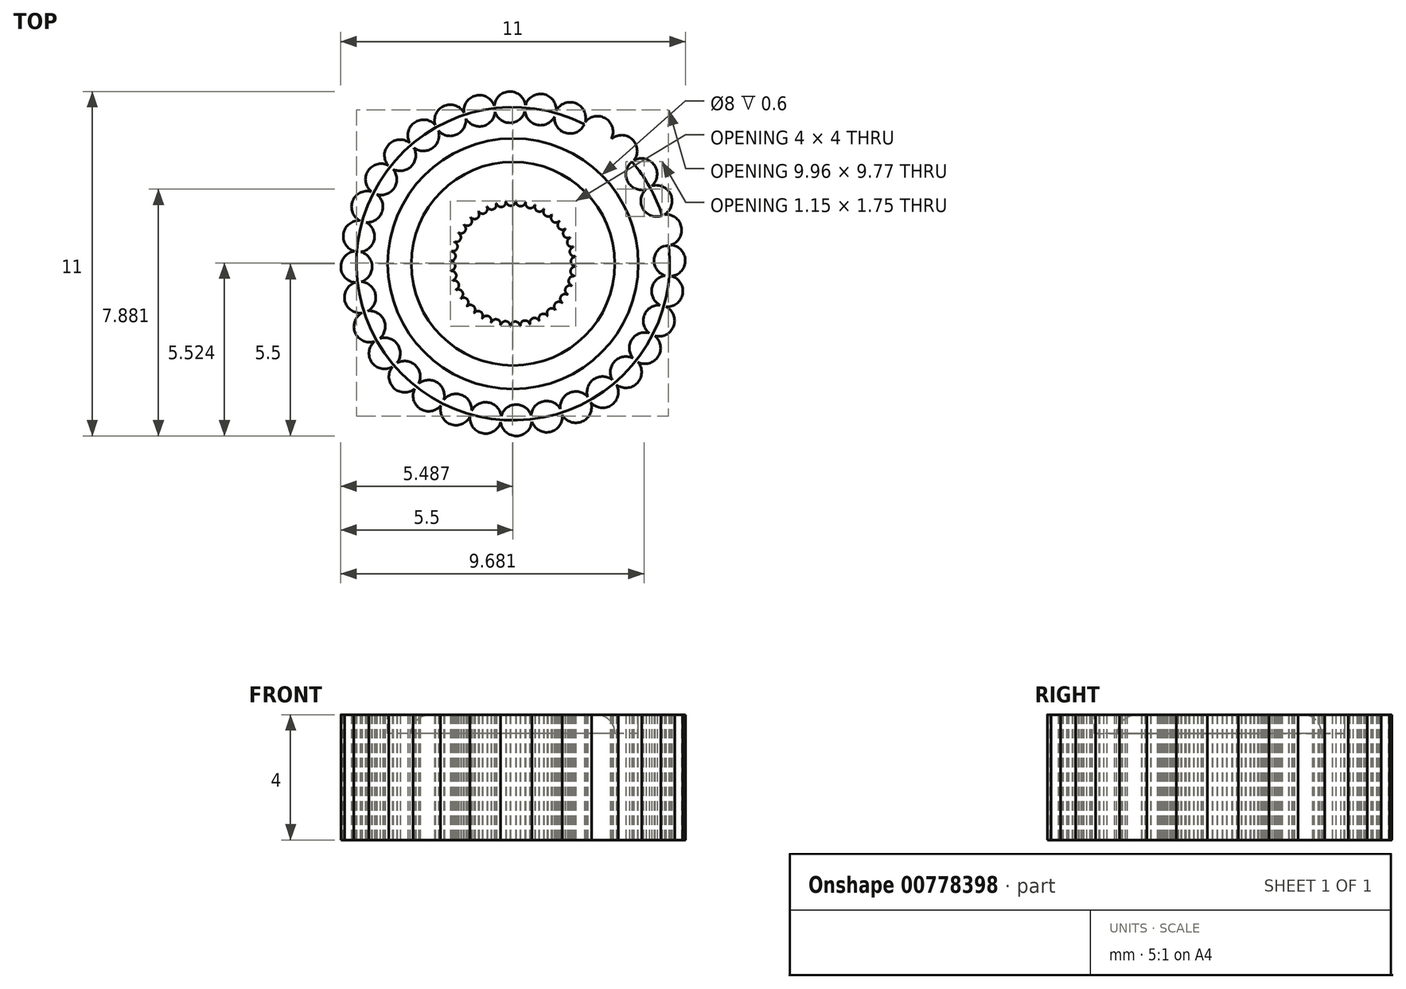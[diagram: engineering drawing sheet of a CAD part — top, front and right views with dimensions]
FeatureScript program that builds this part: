
annotation { "Feature Type Name" : "Feature", "Feature Type Description" : "" }
export const myFeature = defineFeature(function(context is Context, id is Id, definition is map)
    precondition{}
    {
        {
            var Q0;
            Q0=qCreatedBy(makeId("Top.planeOp"),FACE);
            var sketch = newSketch(context, id + "F0", { "sketchPlane" : qUnion([Q0])});
            skCircle(sketch, "E0", {"center": v(0, 0) * mm, "radius": 5 * mm});
            skCircle(sketch, "E1", {"center": v(0, 0) * mm, "radius": 2 * mm});
            skCircle(sketch, "E2", {"center": v(2.7, 4.21) * mm, "radius": 0.5 * mm});
            skCircle(sketch, "E3.1.0", {"center": v(1.82, 4.66) * mm, "radius": 0.5 * mm});
            skCircle(sketch, "E3.2.0", {"center": v(0.88, 4.92) * mm, "radius": 0.5 * mm});
            skCircle(sketch, "E4.1.3.0", {"center": v(-0.1, 5) * mm, "radius": 0.5 * mm});
            skCircle(sketch, "E4.1.4.0", {"center": v(-1.07, 4.88) * mm, "radius": 0.5 * mm});
            skCircle(sketch, "E4.1.5.0", {"center": v(-2, 4.58) * mm, "radius": 0.5 * mm});
            skCircle(sketch, "E4.1.6.0", {"center": v(-2.86, 4.1) * mm, "radius": 0.5 * mm});
            skCircle(sketch, "E4.1.7.0", {"center": v(-3.6, 3.46) * mm, "radius": 0.5 * mm});
            skCircle(sketch, "E4.1.8.0", {"center": v(-4.21, 2.7) * mm, "radius": 0.5 * mm});
            skCircle(sketch, "E4.1.9.0", {"center": v(-4.66, 1.82) * mm, "radius": 0.5 * mm});
            skCircle(sketch, "E5.1.10.0", {"center": v(-4.92, 0.88) * mm, "radius": 0.5 * mm});
            skCircle(sketch, "E5.1.11.0", {"center": v(-5, -0.1) * mm, "radius": 0.5 * mm});
            skCircle(sketch, "E5.1.12.0", {"center": v(-4.88, -1.07) * mm, "radius": 0.5 * mm});
            skCircle(sketch, "E5.1.13.0", {"center": v(-4.58, -2) * mm, "radius": 0.5 * mm});
            skCircle(sketch, "E5.1.14.0", {"center": v(-4.1, -2.86) * mm, "radius": 0.5 * mm});
            skCircle(sketch, "E5.1.15.0", {"center": v(-3.46, -3.6) * mm, "radius": 0.5 * mm});
            skCircle(sketch, "E5.1.16.0", {"center": v(-2.7, -4.21) * mm, "radius": 0.5 * mm});
            skCircle(sketch, "E5.1.17.0", {"center": v(-1.82, -4.66) * mm, "radius": 0.5 * mm});
            skCircle(sketch, "E5.1.18.0", {"center": v(-0.88, -4.92) * mm, "radius": 0.5 * mm});
            skCircle(sketch, "E5.1.19.0", {"center": v(0.1, -5) * mm, "radius": 0.5 * mm});
            skCircle(sketch, "E5.1.20.0", {"center": v(1.07, -4.88) * mm, "radius": 0.5 * mm});
            skCircle(sketch, "E5.1.21.0", {"center": v(2, -4.58) * mm, "radius": 0.5 * mm});
            skCircle(sketch, "E5.1.22.0", {"center": v(2.86, -4.1) * mm, "radius": 0.5 * mm});
            skCircle(sketch, "E5.1.23.0", {"center": v(3.6, -3.46) * mm, "radius": 0.5 * mm});
            skCircle(sketch, "E5.1.24.0", {"center": v(4.21, -2.7) * mm, "radius": 0.5 * mm});
            skCircle(sketch, "E5.1.25.0", {"center": v(4.66, -1.82) * mm, "radius": 0.5 * mm});
            skCircle(sketch, "E5.1.26.0", {"center": v(4.92, -0.88) * mm, "radius": 0.5 * mm});
            skCircle(sketch, "E5.1.27.0", {"center": v(5, 0.1) * mm, "radius": 0.5 * mm});
            skCircle(sketch, "E5.1.28.0", {"center": v(4.88, 1.07) * mm, "radius": 0.5 * mm});
            skCircle(sketch, "E5.1.29.0", {"center": v(4.58, 2) * mm, "radius": 0.5 * mm});
            skCircle(sketch, "E5.1.30.0", {"center": v(4.1, 2.86) * mm, "radius": 0.5 * mm});
            skCircle(sketch, "E5.1.31.0", {"center": v(3.46, 3.6) * mm, "radius": 0.5 * mm});
            skCircle(sketch, "E6", {"center": v(1.36, 1.46) * mm, "radius": 0.15 * mm});
            skCircle(sketch, "E7.1.0", {"center": v(1.12, 1.66) * mm, "radius": 0.15 * mm});
            skCircle(sketch, "E7.2.0", {"center": v(0.84, 1.81) * mm, "radius": 0.15 * mm});
            skCircle(sketch, "E7.3.0", {"center": v(0.55, 1.92) * mm, "radius": 0.15 * mm});
            skCircle(sketch, "E7.4.0", {"center": v(0.24, 1.99) * mm, "radius": 0.15 * mm});
            skCircle(sketch, "E7.5.0", {"center": v(-0.07, 2) * mm, "radius": 0.15 * mm});
            skCircle(sketch, "E7.6.0", {"center": v(-0.38, 1.96) * mm, "radius": 0.15 * mm});
            skCircle(sketch, "E7.7.0", {"center": v(-0.69, 1.88) * mm, "radius": 0.15 * mm});
            skCircle(sketch, "E7.8.0", {"center": v(-0.97, 1.75) * mm, "radius": 0.15 * mm});
            skCircle(sketch, "E7.9.0", {"center": v(-1.23, 1.57) * mm, "radius": 0.15 * mm});
            skCircle(sketch, "E7.10.0", {"center": v(-1.46, 1.36) * mm, "radius": 0.15 * mm});
            skCircle(sketch, "E7.11.0", {"center": v(-1.66, 1.12) * mm, "radius": 0.15 * mm});
            skCircle(sketch, "E7.12.0", {"center": v(-1.81, 0.84) * mm, "radius": 0.15 * mm});
            skCircle(sketch, "E7.13.0", {"center": v(-1.92, 0.55) * mm, "radius": 0.15 * mm});
            skCircle(sketch, "E7.14.0", {"center": v(-1.99, 0.24) * mm, "radius": 0.15 * mm});
            skCircle(sketch, "E7.15.0", {"center": v(-2, -0.07) * mm, "radius": 0.15 * mm});
            skCircle(sketch, "E7.16.0", {"center": v(-1.96, -0.38) * mm, "radius": 0.15 * mm});
            skCircle(sketch, "E7.17.0", {"center": v(-1.88, -0.69) * mm, "radius": 0.15 * mm});
            skCircle(sketch, "E7.18.0", {"center": v(-1.75, -0.97) * mm, "radius": 0.15 * mm});
            skCircle(sketch, "E7.19.0", {"center": v(-1.57, -1.23) * mm, "radius": 0.15 * mm});
            skCircle(sketch, "E8.1.20.0", {"center": v(-1.36, -1.46) * mm, "radius": 0.15 * mm});
            skCircle(sketch, "E8.1.21.0", {"center": v(-1.12, -1.66) * mm, "radius": 0.15 * mm});
            skCircle(sketch, "E8.1.22.0", {"center": v(-0.84, -1.81) * mm, "radius": 0.15 * mm});
            skCircle(sketch, "E8.1.23.0", {"center": v(-0.55, -1.92) * mm, "radius": 0.15 * mm});
            skCircle(sketch, "E8.1.24.0", {"center": v(-0.24, -1.99) * mm, "radius": 0.15 * mm});
            skCircle(sketch, "E8.1.25.0", {"center": v(0.07, -2) * mm, "radius": 0.15 * mm});
            skCircle(sketch, "E8.1.26.0", {"center": v(0.38, -1.96) * mm, "radius": 0.15 * mm});
            skCircle(sketch, "E8.1.27.0", {"center": v(0.69, -1.88) * mm, "radius": 0.15 * mm});
            skCircle(sketch, "E8.1.28.0", {"center": v(0.97, -1.75) * mm, "radius": 0.15 * mm});
            skCircle(sketch, "E8.1.29.0", {"center": v(1.23, -1.57) * mm, "radius": 0.15 * mm});
            skCircle(sketch, "E8.1.30.0", {"center": v(1.46, -1.36) * mm, "radius": 0.15 * mm});
            skCircle(sketch, "E8.1.31.0", {"center": v(1.66, -1.12) * mm, "radius": 0.15 * mm});
            skCircle(sketch, "E8.1.32.0", {"center": v(1.81, -0.84) * mm, "radius": 0.15 * mm});
            skCircle(sketch, "E8.1.33.0", {"center": v(1.92, -0.55) * mm, "radius": 0.15 * mm});
            skCircle(sketch, "E8.1.34.0", {"center": v(1.99, -0.24) * mm, "radius": 0.15 * mm});
            skCircle(sketch, "E8.1.35.0", {"center": v(2, 0.07) * mm, "radius": 0.15 * mm});
            skCircle(sketch, "E8.1.36.0", {"center": v(1.96, 0.38) * mm, "radius": 0.15 * mm});
            skCircle(sketch, "E8.1.37.0", {"center": v(1.88, 0.69) * mm, "radius": 0.15 * mm});
            skCircle(sketch, "E8.1.38.0", {"center": v(1.75, 0.97) * mm, "radius": 0.15 * mm});
            skCircle(sketch, "E8.1.39.0", {"center": v(1.57, 1.23) * mm, "radius": 0.15 * mm});
            skSolve(sketch);
        }
        {
            var Q0;
            {var subQ0=sQuery(id+"F0.wireOp",EDGE,"E5.1.20.0");var subQ1=sQuery(id+"F0.wireOp",EDGE,"E5.1.19.0");var subQ2=makeQuery(id+"F0.imprint","INTERSECT",VERTEX,{"disambiguationData":[OD(0.0)],"derivedFrom":[subQ1,subQ0]});Q0=makeQuery(id+"F0.imprint","IMPRINT",FACE,{"disambiguationData":[TD([[makeQuery(id+"F0.imprint","IMPRINT",EDGE,{"disambiguationData":[TD([[subQ2,-1.0]])],"derivedFrom":subQ1}),-1.0]])]});}
            var Q1;
            {var subQ0=sQuery(id+"F0.wireOp",EDGE,"E4.1.3.0");var subQ1=sQuery(id+"F0.wireOp",EDGE,"E3.2.0");var subQ2=makeQuery(id+"F0.imprint","INTERSECT",VERTEX,{"disambiguationData":[OD(0.0)],"derivedFrom":[subQ1,subQ0]});Q1=makeQuery(id+"F0.imprint","IMPRINT",FACE,{"disambiguationData":[TD([[makeQuery(id+"F0.imprint","IMPRINT",EDGE,{"disambiguationData":[TD([[subQ2,-1.0]])],"derivedFrom":subQ1}),-1.0]])]});}
            var Q2;
            {var subQ0=sQuery(id+"F0.wireOp",EDGE,"E0");var subQ1=sQuery(id+"F0.wireOp",EDGE,"E2");var subQ2=makeQuery(id+"F0.imprint","INTERSECT",VERTEX,{"disambiguationData":[OD(0.0)],"derivedFrom":[subQ1,subQ0]});Q2=makeQuery(id+"F0.imprint","IMPRINT",FACE,{"disambiguationData":[TD([[makeQuery(id+"F0.imprint","IMPRINT",EDGE,{"disambiguationData":[TD([[subQ2,-1.0]])],"derivedFrom":subQ1}),-1.0]])]});}
            var Q3;
            {var subQ0=sQuery(id+"F0.wireOp",EDGE,"E0");var subQ1=sQuery(id+"F0.wireOp",EDGE,"E5.1.13.0");var subQ2=makeQuery(id+"F0.imprint","INTERSECT",VERTEX,{"disambiguationData":[OD(0.0)],"derivedFrom":[subQ1,subQ0]});Q3=makeQuery(id+"F0.imprint","IMPRINT",FACE,{"disambiguationData":[TD([[makeQuery(id+"F0.imprint","IMPRINT",EDGE,{"disambiguationData":[TD([[subQ2,-1.0]])],"derivedFrom":subQ1}),-1.0]])]});}
            var Q4;
            {var subQ0=sQuery(id+"F0.wireOp",EDGE,"E5.1.24.0");var subQ1=sQuery(id+"F0.wireOp",EDGE,"E5.1.23.0");var subQ2=makeQuery(id+"F0.imprint","INTERSECT",VERTEX,{"disambiguationData":[OD(0.0)],"derivedFrom":[subQ1,subQ0]});Q4=makeQuery(id+"F0.imprint","IMPRINT",FACE,{"disambiguationData":[TD([[makeQuery(id+"F0.imprint","IMPRINT",EDGE,{"disambiguationData":[TD([[subQ2,-1.0]])],"derivedFrom":subQ1}),-1.0]])]});}
            var Q5;
            {var subQ0=sQuery(id+"F0.wireOp",EDGE,"E0");var subQ1=sQuery(id+"F0.wireOp",EDGE,"E4.1.8.0");var subQ2=makeQuery(id+"F0.imprint","INTERSECT",VERTEX,{"disambiguationData":[OD(0.0)],"derivedFrom":[subQ1,subQ0]});Q5=makeQuery(id+"F0.imprint","IMPRINT",FACE,{"disambiguationData":[TD([[makeQuery(id+"F0.imprint","IMPRINT",EDGE,{"disambiguationData":[TD([[subQ2,-1.0]])],"derivedFrom":subQ1}),-1.0]])]});}
            var Q6;
            {var subQ0=sQuery(id+"F0.wireOp",EDGE,"E5.1.21.0");var subQ1=sQuery(id+"F0.wireOp",EDGE,"E5.1.20.0");var subQ2=makeQuery(id+"F0.imprint","INTERSECT",VERTEX,{"disambiguationData":[OD(0.0)],"derivedFrom":[subQ1,subQ0]});Q6=makeQuery(id+"F0.imprint","IMPRINT",FACE,{"disambiguationData":[TD([[makeQuery(id+"F0.imprint","IMPRINT",EDGE,{"disambiguationData":[TD([[subQ2,-1.0]])],"derivedFrom":subQ1}),-1.0]])]});}
            var Q7;
            {var subQ0=sQuery(id+"F0.wireOp",EDGE,"E3.1.0");var subQ1=sQuery(id+"F0.wireOp",EDGE,"E2");var subQ2=makeQuery(id+"F0.imprint","INTERSECT",VERTEX,{"disambiguationData":[OD(0.0)],"derivedFrom":[subQ1,subQ0]});Q7=makeQuery(id+"F0.imprint","IMPRINT",FACE,{"disambiguationData":[TD([[makeQuery(id+"F0.imprint","IMPRINT",EDGE,{"disambiguationData":[TD([[subQ2,-1.0]])],"derivedFrom":subQ1}),-1.0]])]});}
            var Q8;
            {var subQ0=sQuery(id+"F0.wireOp",EDGE,"E0");var subQ1=sQuery(id+"F0.wireOp",EDGE,"E5.1.11.0");var subQ2=makeQuery(id+"F0.imprint","INTERSECT",VERTEX,{"disambiguationData":[OD(0.0)],"derivedFrom":[subQ1,subQ0]});Q8=makeQuery(id+"F0.imprint","IMPRINT",FACE,{"disambiguationData":[TD([[makeQuery(id+"F0.imprint","IMPRINT",EDGE,{"disambiguationData":[TD([[subQ2,-1.0]])],"derivedFrom":subQ1}),-1.0]])]});}
            var Q9;
            {var subQ0=sQuery(id+"F0.wireOp",EDGE,"E5.1.11.0");var subQ1=sQuery(id+"F0.wireOp",EDGE,"E5.1.10.0");var subQ2=makeQuery(id+"F0.imprint","INTERSECT",VERTEX,{"disambiguationData":[OD(0.0)],"derivedFrom":[subQ1,subQ0]});Q9=makeQuery(id+"F0.imprint","IMPRINT",FACE,{"disambiguationData":[TD([[makeQuery(id+"F0.imprint","IMPRINT",EDGE,{"disambiguationData":[TD([[subQ2,-1.0]])],"derivedFrom":subQ1}),-1.0]])]});}
            var Q10;
            {var subQ0=sQuery(id+"F0.wireOp",EDGE,"E0");var subQ1=sQuery(id+"F0.wireOp",EDGE,"E5.1.17.0");var subQ2=makeQuery(id+"F0.imprint","INTERSECT",VERTEX,{"disambiguationData":[OD(0.0)],"derivedFrom":[subQ1,subQ0]});Q10=makeQuery(id+"F0.imprint","IMPRINT",FACE,{"disambiguationData":[TD([[makeQuery(id+"F0.imprint","IMPRINT",EDGE,{"disambiguationData":[TD([[subQ2,-1.0]])],"derivedFrom":subQ1}),-1.0]])]});}
            var Q11;
            {var subQ0=sQuery(id+"F0.wireOp",EDGE,"E5.1.14.0");var subQ1=sQuery(id+"F0.wireOp",EDGE,"E5.1.13.0");var subQ2=makeQuery(id+"F0.imprint","INTERSECT",VERTEX,{"disambiguationData":[OD(0.0)],"derivedFrom":[subQ1,subQ0]});Q11=makeQuery(id+"F0.imprint","IMPRINT",FACE,{"disambiguationData":[TD([[makeQuery(id+"F0.imprint","IMPRINT",EDGE,{"disambiguationData":[TD([[subQ2,-1.0]])],"derivedFrom":subQ1}),-1.0]])]});}
            var Q12;
            {var subQ0=sQuery(id+"F0.wireOp",EDGE,"E0");var subQ1=sQuery(id+"F0.wireOp",EDGE,"E5.1.20.0");var subQ2=makeQuery(id+"F0.imprint","INTERSECT",VERTEX,{"disambiguationData":[OD(0.0)],"derivedFrom":[subQ1,subQ0]});Q12=makeQuery(id+"F0.imprint","IMPRINT",FACE,{"disambiguationData":[TD([[makeQuery(id+"F0.imprint","IMPRINT",EDGE,{"disambiguationData":[TD([[subQ2,-1.0]])],"derivedFrom":subQ1}),-1.0]])]});}
            var Q13;
            {var subQ0=sQuery(id+"F0.wireOp",EDGE,"E0");var subQ1=sQuery(id+"F0.wireOp",EDGE,"E4.1.5.0");var subQ2=makeQuery(id+"F0.imprint","INTERSECT",VERTEX,{"disambiguationData":[OD(0.0)],"derivedFrom":[subQ1,subQ0]});Q13=makeQuery(id+"F0.imprint","IMPRINT",FACE,{"disambiguationData":[TD([[makeQuery(id+"F0.imprint","IMPRINT",EDGE,{"disambiguationData":[TD([[subQ2,-1.0]])],"derivedFrom":subQ1}),-1.0]])]});}
            var Q14;
            {var subQ131=sQuery(id+"F0.wireOp",EDGE,"E3.1.0");var subQ138=sQuery(id+"F0.wireOp",EDGE,"E2");var subQ139=makeQuery(id+"F0.imprint","INTERSECT",VERTEX,{"disambiguationData":[OD(1.0)],"derivedFrom":[subQ138,subQ131]});Q14=makeQuery(id+"F0.imprint","IMPRINT",FACE,{"disambiguationData":[TD([[makeQuery(id+"F0.imprint","IMPRINT",EDGE,{"disambiguationData":[TD([[subQ139,-1.0]])],"derivedFrom":subQ138}),-1.0]])]});}
            var Q15;
            {var subQ0=sQuery(id+"F0.wireOp",EDGE,"E0");var subQ1=sQuery(id+"F0.wireOp",EDGE,"E5.1.22.0");var subQ2=makeQuery(id+"F0.imprint","INTERSECT",VERTEX,{"disambiguationData":[OD(0.0)],"derivedFrom":[subQ1,subQ0]});Q15=makeQuery(id+"F0.imprint","IMPRINT",FACE,{"disambiguationData":[TD([[makeQuery(id+"F0.imprint","IMPRINT",EDGE,{"disambiguationData":[TD([[subQ2,-1.0]])],"derivedFrom":subQ1}),-1.0]])]});}
            var Q16;
            {var subQ0=sQuery(id+"F0.wireOp",EDGE,"E0");var subQ1=sQuery(id+"F0.wireOp",EDGE,"E3.2.0");var subQ2=makeQuery(id+"F0.imprint","INTERSECT",VERTEX,{"disambiguationData":[OD(0.0)],"derivedFrom":[subQ1,subQ0]});Q16=makeQuery(id+"F0.imprint","IMPRINT",FACE,{"disambiguationData":[TD([[makeQuery(id+"F0.imprint","IMPRINT",EDGE,{"disambiguationData":[TD([[subQ2,-1.0]])],"derivedFrom":subQ1}),1.0]])]});}
            var Q17;
            {var subQ0=sQuery(id+"F0.wireOp",EDGE,"E0");var subQ1=sQuery(id+"F0.wireOp",EDGE,"E4.1.9.0");var subQ2=makeQuery(id+"F0.imprint","INTERSECT",VERTEX,{"disambiguationData":[OD(0.0)],"derivedFrom":[subQ1,subQ0]});Q17=makeQuery(id+"F0.imprint","IMPRINT",FACE,{"disambiguationData":[TD([[makeQuery(id+"F0.imprint","IMPRINT",EDGE,{"disambiguationData":[TD([[subQ2,-1.0]])],"derivedFrom":subQ1}),-1.0]])]});}
            var Q18;
            {var subQ0=sQuery(id+"F0.wireOp",EDGE,"E0");var subQ1=sQuery(id+"F0.wireOp",EDGE,"E5.1.10.0");var subQ2=makeQuery(id+"F0.imprint","INTERSECT",VERTEX,{"disambiguationData":[OD(0.0)],"derivedFrom":[subQ1,subQ0]});Q18=makeQuery(id+"F0.imprint","IMPRINT",FACE,{"disambiguationData":[TD([[makeQuery(id+"F0.imprint","IMPRINT",EDGE,{"disambiguationData":[TD([[subQ2,-1.0]])],"derivedFrom":subQ1}),-1.0]])]});}
            var Q19;
            {var subQ0=sQuery(id+"F0.wireOp",EDGE,"E5.1.31.0");var subQ1=sQuery(id+"F0.wireOp",EDGE,"E2");var subQ2=makeQuery(id+"F0.imprint","INTERSECT",VERTEX,{"disambiguationData":[OD(1.0)],"derivedFrom":[subQ1,subQ0]});Q19=makeQuery(id+"F0.imprint","IMPRINT",FACE,{"disambiguationData":[TD([[makeQuery(id+"F0.imprint","IMPRINT",EDGE,{"disambiguationData":[TD([[subQ2,-1.0]])],"derivedFrom":subQ1}),-1.0]])]});}
            var Q20;
            {var subQ0=sQuery(id+"F0.wireOp",EDGE,"E0");var subQ1=sQuery(id+"F0.wireOp",EDGE,"E5.1.14.0");var subQ2=makeQuery(id+"F0.imprint","INTERSECT",VERTEX,{"disambiguationData":[OD(0.0)],"derivedFrom":[subQ1,subQ0]});Q20=makeQuery(id+"F0.imprint","IMPRINT",FACE,{"disambiguationData":[TD([[makeQuery(id+"F0.imprint","IMPRINT",EDGE,{"disambiguationData":[TD([[subQ2,-1.0]])],"derivedFrom":subQ1}),-1.0]])]});}
            var Q21;
            {var subQ0=sQuery(id+"F0.wireOp",EDGE,"E4.1.7.0");var subQ1=sQuery(id+"F0.wireOp",EDGE,"E4.1.6.0");var subQ2=makeQuery(id+"F0.imprint","INTERSECT",VERTEX,{"disambiguationData":[OD(0.0)],"derivedFrom":[subQ1,subQ0]});Q21=makeQuery(id+"F0.imprint","IMPRINT",FACE,{"disambiguationData":[TD([[makeQuery(id+"F0.imprint","IMPRINT",EDGE,{"disambiguationData":[TD([[subQ2,-1.0]])],"derivedFrom":subQ1}),-1.0]])]});}
            var Q22;
            {var subQ0=sQuery(id+"F0.wireOp",EDGE,"E0");var subQ1=sQuery(id+"F0.wireOp",EDGE,"E5.1.23.0");var subQ2=makeQuery(id+"F0.imprint","INTERSECT",VERTEX,{"disambiguationData":[OD(0.0)],"derivedFrom":[subQ1,subQ0]});Q22=makeQuery(id+"F0.imprint","IMPRINT",FACE,{"disambiguationData":[TD([[makeQuery(id+"F0.imprint","IMPRINT",EDGE,{"disambiguationData":[TD([[subQ2,-1.0]])],"derivedFrom":subQ1}),-1.0]])]});}
            var Q23;
            {var subQ0=sQuery(id+"F0.wireOp",EDGE,"E0");var subQ1=sQuery(id+"F0.wireOp",EDGE,"E5.1.29.0");var subQ2=makeQuery(id+"F0.imprint","INTERSECT",VERTEX,{"disambiguationData":[OD(0.0)],"derivedFrom":[subQ1,subQ0]});Q23=makeQuery(id+"F0.imprint","IMPRINT",FACE,{"disambiguationData":[TD([[makeQuery(id+"F0.imprint","IMPRINT",EDGE,{"disambiguationData":[TD([[subQ2,-1.0]])],"derivedFrom":subQ1}),-1.0]])]});}
            var Q24;
            {var subQ0=sQuery(id+"F0.wireOp",EDGE,"E4.1.9.0");var subQ1=sQuery(id+"F0.wireOp",EDGE,"E4.1.8.0");var subQ2=makeQuery(id+"F0.imprint","INTERSECT",VERTEX,{"disambiguationData":[OD(0.0)],"derivedFrom":[subQ1,subQ0]});Q24=makeQuery(id+"F0.imprint","IMPRINT",FACE,{"disambiguationData":[TD([[makeQuery(id+"F0.imprint","IMPRINT",EDGE,{"disambiguationData":[TD([[subQ2,-1.0]])],"derivedFrom":subQ1}),-1.0]])]});}
            var Q25;
            {var subQ0=sQuery(id+"F0.wireOp",EDGE,"E5.1.10.0");var subQ1=sQuery(id+"F0.wireOp",EDGE,"E4.1.9.0");var subQ2=makeQuery(id+"F0.imprint","INTERSECT",VERTEX,{"disambiguationData":[OD(0.0)],"derivedFrom":[subQ1,subQ0]});Q25=makeQuery(id+"F0.imprint","IMPRINT",FACE,{"disambiguationData":[TD([[makeQuery(id+"F0.imprint","IMPRINT",EDGE,{"disambiguationData":[TD([[subQ2,-1.0]])],"derivedFrom":subQ1}),-1.0]])]});}
            var Q26;
            {var subQ0=sQuery(id+"F0.wireOp",EDGE,"E5.1.30.0");var subQ1=sQuery(id+"F0.wireOp",EDGE,"E5.1.29.0");var subQ2=makeQuery(id+"F0.imprint","INTERSECT",VERTEX,{"disambiguationData":[OD(0.0)],"derivedFrom":[subQ1,subQ0]});Q26=makeQuery(id+"F0.imprint","IMPRINT",FACE,{"disambiguationData":[TD([[makeQuery(id+"F0.imprint","IMPRINT",EDGE,{"disambiguationData":[TD([[subQ2,-1.0]])],"derivedFrom":subQ1}),-1.0]])]});}
            var Q27;
            {var subQ0=sQuery(id+"F0.wireOp",EDGE,"E0");var subQ1=sQuery(id+"F0.wireOp",EDGE,"E5.1.13.0");var subQ2=makeQuery(id+"F0.imprint","INTERSECT",VERTEX,{"disambiguationData":[OD(0.0)],"derivedFrom":[subQ1,subQ0]});Q27=makeQuery(id+"F0.imprint","IMPRINT",FACE,{"disambiguationData":[TD([[makeQuery(id+"F0.imprint","IMPRINT",EDGE,{"disambiguationData":[TD([[subQ2,-1.0]])],"derivedFrom":subQ1}),1.0]])]});}
            var Q28;
            {var subQ0=sQuery(id+"F0.wireOp",EDGE,"E3.1.0");var subQ1=sQuery(id+"F0.wireOp",EDGE,"E2");var subQ2=makeQuery(id+"F0.imprint","INTERSECT",VERTEX,{"disambiguationData":[OD(1.0)],"derivedFrom":[subQ1,subQ0]});Q28=makeQuery(id+"F0.imprint","IMPRINT",FACE,{"disambiguationData":[TD([[makeQuery(id+"F0.imprint","IMPRINT",EDGE,{"disambiguationData":[TD([[subQ2,-1.0]])],"derivedFrom":subQ1}),1.0]])]});}
            var Q29;
            {var subQ0=sQuery(id+"F0.wireOp",EDGE,"E5.1.20.0");var subQ1=sQuery(id+"F0.wireOp",EDGE,"E5.1.19.0");var subQ2=makeQuery(id+"F0.imprint","INTERSECT",VERTEX,{"disambiguationData":[OD(0.0)],"derivedFrom":[subQ1,subQ0]});Q29=makeQuery(id+"F0.imprint","IMPRINT",FACE,{"disambiguationData":[TD([[makeQuery(id+"F0.imprint","IMPRINT",EDGE,{"disambiguationData":[TD([[subQ2,-1.0]])],"derivedFrom":subQ1}),1.0]])]});}
            var Q30;
            {var subQ0=sQuery(id+"F0.wireOp",EDGE,"E0");var subQ1=sQuery(id+"F0.wireOp",EDGE,"E5.1.15.0");var subQ2=makeQuery(id+"F0.imprint","INTERSECT",VERTEX,{"disambiguationData":[OD(0.0)],"derivedFrom":[subQ1,subQ0]});Q30=makeQuery(id+"F0.imprint","IMPRINT",FACE,{"disambiguationData":[TD([[makeQuery(id+"F0.imprint","IMPRINT",EDGE,{"disambiguationData":[TD([[subQ2,-1.0]])],"derivedFrom":subQ1}),-1.0]])]});}
            var Q31;
            {var subQ0=sQuery(id+"F0.wireOp",EDGE,"E0");var subQ1=sQuery(id+"F0.wireOp",EDGE,"E5.1.24.0");var subQ2=makeQuery(id+"F0.imprint","INTERSECT",VERTEX,{"disambiguationData":[OD(0.0)],"derivedFrom":[subQ1,subQ0]});Q31=makeQuery(id+"F0.imprint","IMPRINT",FACE,{"disambiguationData":[TD([[makeQuery(id+"F0.imprint","IMPRINT",EDGE,{"disambiguationData":[TD([[subQ2,-1.0]])],"derivedFrom":subQ1}),-1.0]])]});}
            var Q32;
            {var subQ0=sQuery(id+"F0.wireOp",EDGE,"E5.1.19.0");var subQ1=sQuery(id+"F0.wireOp",EDGE,"E5.1.18.0");var subQ2=makeQuery(id+"F0.imprint","INTERSECT",VERTEX,{"disambiguationData":[OD(0.0)],"derivedFrom":[subQ1,subQ0]});Q32=makeQuery(id+"F0.imprint","IMPRINT",FACE,{"disambiguationData":[TD([[makeQuery(id+"F0.imprint","IMPRINT",EDGE,{"disambiguationData":[TD([[subQ2,-1.0]])],"derivedFrom":subQ1}),1.0]])]});}
            var Q33;
            {var subQ0=sQuery(id+"F0.wireOp",EDGE,"E0");var subQ1=sQuery(id+"F0.wireOp",EDGE,"E5.1.28.0");var subQ2=makeQuery(id+"F0.imprint","INTERSECT",VERTEX,{"disambiguationData":[OD(0.0)],"derivedFrom":[subQ1,subQ0]});Q33=makeQuery(id+"F0.imprint","IMPRINT",FACE,{"disambiguationData":[TD([[makeQuery(id+"F0.imprint","IMPRINT",EDGE,{"disambiguationData":[TD([[subQ2,-1.0]])],"derivedFrom":subQ1}),1.0]])]});}
            var Q34;
            {var subQ0=sQuery(id+"F0.wireOp",EDGE,"E4.1.5.0");var subQ1=sQuery(id+"F0.wireOp",EDGE,"E4.1.4.0");var subQ2=makeQuery(id+"F0.imprint","INTERSECT",VERTEX,{"disambiguationData":[OD(0.0)],"derivedFrom":[subQ1,subQ0]});Q34=makeQuery(id+"F0.imprint","IMPRINT",FACE,{"disambiguationData":[TD([[makeQuery(id+"F0.imprint","IMPRINT",EDGE,{"disambiguationData":[TD([[subQ2,-1.0]])],"derivedFrom":subQ1}),-1.0]])]});}
            var Q35;
            {var subQ0=sQuery(id+"F0.wireOp",EDGE,"E5.1.25.0");var subQ1=sQuery(id+"F0.wireOp",EDGE,"E5.1.24.0");var subQ2=makeQuery(id+"F0.imprint","INTERSECT",VERTEX,{"disambiguationData":[OD(0.0)],"derivedFrom":[subQ1,subQ0]});Q35=makeQuery(id+"F0.imprint","IMPRINT",FACE,{"disambiguationData":[TD([[makeQuery(id+"F0.imprint","IMPRINT",EDGE,{"disambiguationData":[TD([[subQ2,-1.0]])],"derivedFrom":subQ1}),-1.0]])]});}
            var Q36;
            {var subQ0=sQuery(id+"F0.wireOp",EDGE,"E0");var subQ1=sQuery(id+"F0.wireOp",EDGE,"E5.1.25.0");var subQ2=makeQuery(id+"F0.imprint","INTERSECT",VERTEX,{"disambiguationData":[OD(0.0)],"derivedFrom":[subQ1,subQ0]});Q36=makeQuery(id+"F0.imprint","IMPRINT",FACE,{"disambiguationData":[TD([[makeQuery(id+"F0.imprint","IMPRINT",EDGE,{"disambiguationData":[TD([[subQ2,-1.0]])],"derivedFrom":subQ1}),-1.0]])]});}
            var Q37;
            {var subQ0=sQuery(id+"F0.wireOp",EDGE,"E0");var subQ1=sQuery(id+"F0.wireOp",EDGE,"E5.1.29.0");var subQ2=makeQuery(id+"F0.imprint","INTERSECT",VERTEX,{"disambiguationData":[OD(0.0)],"derivedFrom":[subQ1,subQ0]});Q37=makeQuery(id+"F0.imprint","IMPRINT",FACE,{"disambiguationData":[TD([[makeQuery(id+"F0.imprint","IMPRINT",EDGE,{"disambiguationData":[TD([[subQ2,-1.0]])],"derivedFrom":subQ1}),1.0]])]});}
            var Q38;
            {var subQ0=sQuery(id+"F0.wireOp",EDGE,"E5.1.19.0");var subQ1=sQuery(id+"F0.wireOp",EDGE,"E5.1.18.0");var subQ2=makeQuery(id+"F0.imprint","INTERSECT",VERTEX,{"disambiguationData":[OD(0.0)],"derivedFrom":[subQ1,subQ0]});Q38=makeQuery(id+"F0.imprint","IMPRINT",FACE,{"disambiguationData":[TD([[makeQuery(id+"F0.imprint","IMPRINT",EDGE,{"disambiguationData":[TD([[subQ2,-1.0]])],"derivedFrom":subQ1}),-1.0]])]});}
            var Q39;
            {var subQ0=sQuery(id+"F0.wireOp",EDGE,"E0");var subQ1=sQuery(id+"F0.wireOp",EDGE,"E5.1.27.0");var subQ2=makeQuery(id+"F0.imprint","INTERSECT",VERTEX,{"disambiguationData":[OD(0.0)],"derivedFrom":[subQ1,subQ0]});Q39=makeQuery(id+"F0.imprint","IMPRINT",FACE,{"disambiguationData":[TD([[makeQuery(id+"F0.imprint","IMPRINT",EDGE,{"disambiguationData":[TD([[subQ2,-1.0]])],"derivedFrom":subQ1}),-1.0]])]});}
            var Q40;
            {var subQ0=sQuery(id+"F0.wireOp",EDGE,"E5.1.26.0");var subQ1=sQuery(id+"F0.wireOp",EDGE,"E5.1.25.0");var subQ2=makeQuery(id+"F0.imprint","INTERSECT",VERTEX,{"disambiguationData":[OD(0.0)],"derivedFrom":[subQ1,subQ0]});Q40=makeQuery(id+"F0.imprint","IMPRINT",FACE,{"disambiguationData":[TD([[makeQuery(id+"F0.imprint","IMPRINT",EDGE,{"disambiguationData":[TD([[subQ2,-1.0]])],"derivedFrom":subQ1}),-1.0]])]});}
            var Q41;
            {var subQ0=sQuery(id+"F0.wireOp",EDGE,"E0");var subQ1=sQuery(id+"F0.wireOp",EDGE,"E5.1.20.0");var subQ2=makeQuery(id+"F0.imprint","INTERSECT",VERTEX,{"disambiguationData":[OD(0.0)],"derivedFrom":[subQ1,subQ0]});Q41=makeQuery(id+"F0.imprint","IMPRINT",FACE,{"disambiguationData":[TD([[makeQuery(id+"F0.imprint","IMPRINT",EDGE,{"disambiguationData":[TD([[subQ2,-1.0]])],"derivedFrom":subQ1}),1.0]])]});}
            var Q42;
            {var subQ0=sQuery(id+"F0.wireOp",EDGE,"E5.1.16.0");var subQ1=sQuery(id+"F0.wireOp",EDGE,"E5.1.15.0");var subQ2=makeQuery(id+"F0.imprint","INTERSECT",VERTEX,{"disambiguationData":[OD(0.0)],"derivedFrom":[subQ1,subQ0]});Q42=makeQuery(id+"F0.imprint","IMPRINT",FACE,{"disambiguationData":[TD([[makeQuery(id+"F0.imprint","IMPRINT",EDGE,{"disambiguationData":[TD([[subQ2,-1.0]])],"derivedFrom":subQ1}),-1.0]])]});}
            var Q43;
            {var subQ0=sQuery(id+"F0.wireOp",EDGE,"E0");var subQ1=sQuery(id+"F0.wireOp",EDGE,"E4.1.4.0");var subQ2=makeQuery(id+"F0.imprint","INTERSECT",VERTEX,{"disambiguationData":[OD(0.0)],"derivedFrom":[subQ1,subQ0]});Q43=makeQuery(id+"F0.imprint","IMPRINT",FACE,{"disambiguationData":[TD([[makeQuery(id+"F0.imprint","IMPRINT",EDGE,{"disambiguationData":[TD([[subQ2,-1.0]])],"derivedFrom":subQ1}),1.0]])]});}
            var Q44;
            {var subQ0=sQuery(id+"F0.wireOp",EDGE,"E0");var subQ1=sQuery(id+"F0.wireOp",EDGE,"E4.1.8.0");var subQ2=makeQuery(id+"F0.imprint","INTERSECT",VERTEX,{"disambiguationData":[OD(0.0)],"derivedFrom":[subQ1,subQ0]});Q44=makeQuery(id+"F0.imprint","IMPRINT",FACE,{"disambiguationData":[TD([[makeQuery(id+"F0.imprint","IMPRINT",EDGE,{"disambiguationData":[TD([[subQ2,-1.0]])],"derivedFrom":subQ1}),1.0]])]});}
            var Q45;
            {var subQ0=sQuery(id+"F0.wireOp",EDGE,"E4.1.4.0");var subQ1=sQuery(id+"F0.wireOp",EDGE,"E4.1.3.0");var subQ2=makeQuery(id+"F0.imprint","INTERSECT",VERTEX,{"disambiguationData":[OD(0.0)],"derivedFrom":[subQ1,subQ0]});Q45=makeQuery(id+"F0.imprint","IMPRINT",FACE,{"disambiguationData":[TD([[makeQuery(id+"F0.imprint","IMPRINT",EDGE,{"disambiguationData":[TD([[subQ2,-1.0]])],"derivedFrom":subQ1}),-1.0]])]});}
            var Q46;
            {var subQ0=sQuery(id+"F0.wireOp",EDGE,"E0");var subQ1=sQuery(id+"F0.wireOp",EDGE,"E5.1.28.0");var subQ2=makeQuery(id+"F0.imprint","INTERSECT",VERTEX,{"disambiguationData":[OD(0.0)],"derivedFrom":[subQ1,subQ0]});Q46=makeQuery(id+"F0.imprint","IMPRINT",FACE,{"disambiguationData":[TD([[makeQuery(id+"F0.imprint","IMPRINT",EDGE,{"disambiguationData":[TD([[subQ2,-1.0]])],"derivedFrom":subQ1}),-1.0]])]});}
            var Q47;
            {var subQ0=sQuery(id+"F0.wireOp",EDGE,"E0");var subQ1=sQuery(id+"F0.wireOp",EDGE,"E5.1.12.0");var subQ2=makeQuery(id+"F0.imprint","INTERSECT",VERTEX,{"disambiguationData":[OD(0.0)],"derivedFrom":[subQ1,subQ0]});Q47=makeQuery(id+"F0.imprint","IMPRINT",FACE,{"disambiguationData":[TD([[makeQuery(id+"F0.imprint","IMPRINT",EDGE,{"disambiguationData":[TD([[subQ2,-1.0]])],"derivedFrom":subQ1}),-1.0]])]});}
            var Q48;
            {var subQ0=sQuery(id+"F0.wireOp",EDGE,"E0");var subQ1=sQuery(id+"F0.wireOp",EDGE,"E3.1.0");var subQ2=makeQuery(id+"F0.imprint","INTERSECT",VERTEX,{"disambiguationData":[OD(0.0)],"derivedFrom":[subQ1,subQ0]});Q48=makeQuery(id+"F0.imprint","IMPRINT",FACE,{"disambiguationData":[TD([[makeQuery(id+"F0.imprint","IMPRINT",EDGE,{"disambiguationData":[TD([[subQ2,-1.0]])],"derivedFrom":subQ1}),-1.0]])]});}
            var Q49;
            {var subQ0=sQuery(id+"F0.wireOp",EDGE,"E5.1.31.0");var subQ1=sQuery(id+"F0.wireOp",EDGE,"E5.1.30.0");var subQ2=makeQuery(id+"F0.imprint","INTERSECT",VERTEX,{"disambiguationData":[OD(0.0)],"derivedFrom":[subQ1,subQ0]});Q49=makeQuery(id+"F0.imprint","IMPRINT",FACE,{"disambiguationData":[TD([[makeQuery(id+"F0.imprint","IMPRINT",EDGE,{"disambiguationData":[TD([[subQ2,-1.0]])],"derivedFrom":subQ1}),1.0]])]});}
            var Q50;
            {var subQ0=sQuery(id+"F0.wireOp",EDGE,"E5.1.27.0");var subQ1=sQuery(id+"F0.wireOp",EDGE,"E5.1.26.0");var subQ2=makeQuery(id+"F0.imprint","INTERSECT",VERTEX,{"disambiguationData":[OD(0.0)],"derivedFrom":[subQ1,subQ0]});Q50=makeQuery(id+"F0.imprint","IMPRINT",FACE,{"disambiguationData":[TD([[makeQuery(id+"F0.imprint","IMPRINT",EDGE,{"disambiguationData":[TD([[subQ2,-1.0]])],"derivedFrom":subQ1}),-1.0]])]});}
            var Q51;
            {var subQ0=sQuery(id+"F0.wireOp",EDGE,"E5.1.25.0");var subQ1=sQuery(id+"F0.wireOp",EDGE,"E5.1.24.0");var subQ2=makeQuery(id+"F0.imprint","INTERSECT",VERTEX,{"disambiguationData":[OD(0.0)],"derivedFrom":[subQ1,subQ0]});Q51=makeQuery(id+"F0.imprint","IMPRINT",FACE,{"disambiguationData":[TD([[makeQuery(id+"F0.imprint","IMPRINT",EDGE,{"disambiguationData":[TD([[subQ2,-1.0]])],"derivedFrom":subQ1}),1.0]])]});}
            var Q52;
            {var subQ0=sQuery(id+"F0.wireOp",EDGE,"E0");var subQ1=sQuery(id+"F0.wireOp",EDGE,"E5.1.14.0");var subQ2=makeQuery(id+"F0.imprint","INTERSECT",VERTEX,{"disambiguationData":[OD(0.0)],"derivedFrom":[subQ1,subQ0]});Q52=makeQuery(id+"F0.imprint","IMPRINT",FACE,{"disambiguationData":[TD([[makeQuery(id+"F0.imprint","IMPRINT",EDGE,{"disambiguationData":[TD([[subQ2,-1.0]])],"derivedFrom":subQ1}),1.0]])]});}
            var Q53;
            {var subQ0=sQuery(id+"F0.wireOp",EDGE,"E5.1.31.0");var subQ1=sQuery(id+"F0.wireOp",EDGE,"E2");var subQ2=makeQuery(id+"F0.imprint","INTERSECT",VERTEX,{"disambiguationData":[OD(0.0)],"derivedFrom":[subQ1,subQ0]});Q53=makeQuery(id+"F0.imprint","IMPRINT",FACE,{"disambiguationData":[TD([[makeQuery(id+"F0.imprint","IMPRINT",EDGE,{"disambiguationData":[TD([[subQ2,1.0]])],"derivedFrom":subQ1}),-1.0]])]});}
            var Q54;
            {var subQ0=sQuery(id+"F0.wireOp",EDGE,"E5.1.22.0");var subQ1=sQuery(id+"F0.wireOp",EDGE,"E5.1.21.0");var subQ2=makeQuery(id+"F0.imprint","INTERSECT",VERTEX,{"disambiguationData":[OD(0.0)],"derivedFrom":[subQ1,subQ0]});Q54=makeQuery(id+"F0.imprint","IMPRINT",FACE,{"disambiguationData":[TD([[makeQuery(id+"F0.imprint","IMPRINT",EDGE,{"disambiguationData":[TD([[subQ2,-1.0]])],"derivedFrom":subQ1}),-1.0]])]});}
            var Q55;
            {var subQ0=sQuery(id+"F0.wireOp",EDGE,"E4.1.6.0");var subQ1=sQuery(id+"F0.wireOp",EDGE,"E4.1.5.0");var subQ2=makeQuery(id+"F0.imprint","INTERSECT",VERTEX,{"disambiguationData":[OD(0.0)],"derivedFrom":[subQ1,subQ0]});Q55=makeQuery(id+"F0.imprint","IMPRINT",FACE,{"disambiguationData":[TD([[makeQuery(id+"F0.imprint","IMPRINT",EDGE,{"disambiguationData":[TD([[subQ2,-1.0]])],"derivedFrom":subQ1}),-1.0]])]});}
            var Q56;
            {var subQ0=sQuery(id+"F0.wireOp",EDGE,"E0");var subQ1=sQuery(id+"F0.wireOp",EDGE,"E5.1.18.0");var subQ2=makeQuery(id+"F0.imprint","INTERSECT",VERTEX,{"disambiguationData":[OD(0.0)],"derivedFrom":[subQ1,subQ0]});Q56=makeQuery(id+"F0.imprint","IMPRINT",FACE,{"disambiguationData":[TD([[makeQuery(id+"F0.imprint","IMPRINT",EDGE,{"disambiguationData":[TD([[subQ2,-1.0]])],"derivedFrom":subQ1}),-1.0]])]});}
            var Q57;
            {var subQ0=sQuery(id+"F0.wireOp",EDGE,"E0");var subQ1=sQuery(id+"F0.wireOp",EDGE,"E3.2.0");var subQ2=makeQuery(id+"F0.imprint","INTERSECT",VERTEX,{"disambiguationData":[OD(0.0)],"derivedFrom":[subQ1,subQ0]});Q57=makeQuery(id+"F0.imprint","IMPRINT",FACE,{"disambiguationData":[TD([[makeQuery(id+"F0.imprint","IMPRINT",EDGE,{"disambiguationData":[TD([[subQ2,-1.0]])],"derivedFrom":subQ1}),-1.0]])]});}
            var Q58;
            {var subQ0=sQuery(id+"F0.wireOp",EDGE,"E5.1.28.0");var subQ1=sQuery(id+"F0.wireOp",EDGE,"E5.1.27.0");var subQ2=makeQuery(id+"F0.imprint","INTERSECT",VERTEX,{"disambiguationData":[OD(0.0)],"derivedFrom":[subQ1,subQ0]});Q58=makeQuery(id+"F0.imprint","IMPRINT",FACE,{"disambiguationData":[TD([[makeQuery(id+"F0.imprint","IMPRINT",EDGE,{"disambiguationData":[TD([[subQ2,-1.0]])],"derivedFrom":subQ1}),-1.0]])]});}
            var Q59;
            {var subQ0=sQuery(id+"F0.wireOp",EDGE,"E0");var subQ1=sQuery(id+"F0.wireOp",EDGE,"E4.1.4.0");var subQ2=makeQuery(id+"F0.imprint","INTERSECT",VERTEX,{"disambiguationData":[OD(0.0)],"derivedFrom":[subQ1,subQ0]});Q59=makeQuery(id+"F0.imprint","IMPRINT",FACE,{"disambiguationData":[TD([[makeQuery(id+"F0.imprint","IMPRINT",EDGE,{"disambiguationData":[TD([[subQ2,-1.0]])],"derivedFrom":subQ1}),-1.0]])]});}
            var Q60;
            {var subQ0=sQuery(id+"F0.wireOp",EDGE,"E3.1.0");var subQ1=sQuery(id+"F0.wireOp",EDGE,"E2");var subQ2=makeQuery(id+"F0.imprint","INTERSECT",VERTEX,{"disambiguationData":[OD(0.0)],"derivedFrom":[subQ1,subQ0]});Q60=makeQuery(id+"F0.imprint","IMPRINT",FACE,{"disambiguationData":[TD([[makeQuery(id+"F0.imprint","IMPRINT",EDGE,{"disambiguationData":[TD([[subQ2,1.0]])],"derivedFrom":subQ1}),1.0]])]});}
            var Q61;
            {var subQ0=sQuery(id+"F0.wireOp",EDGE,"E5.1.12.0");var subQ1=sQuery(id+"F0.wireOp",EDGE,"E5.1.11.0");var subQ2=makeQuery(id+"F0.imprint","INTERSECT",VERTEX,{"disambiguationData":[OD(0.0)],"derivedFrom":[subQ1,subQ0]});Q61=makeQuery(id+"F0.imprint","IMPRINT",FACE,{"disambiguationData":[TD([[makeQuery(id+"F0.imprint","IMPRINT",EDGE,{"disambiguationData":[TD([[subQ2,-1.0]])],"derivedFrom":subQ1}),-1.0]])]});}
            var Q62;
            {var subQ0=sQuery(id+"F0.wireOp",EDGE,"E0");var subQ1=sQuery(id+"F0.wireOp",EDGE,"E5.1.21.0");var subQ2=makeQuery(id+"F0.imprint","INTERSECT",VERTEX,{"disambiguationData":[OD(0.0)],"derivedFrom":[subQ1,subQ0]});Q62=makeQuery(id+"F0.imprint","IMPRINT",FACE,{"disambiguationData":[TD([[makeQuery(id+"F0.imprint","IMPRINT",EDGE,{"disambiguationData":[TD([[subQ2,-1.0]])],"derivedFrom":subQ1}),1.0]])]});}
            var Q63;
            {var subQ0=sQuery(id+"F0.wireOp",EDGE,"E5.1.17.0");var subQ1=sQuery(id+"F0.wireOp",EDGE,"E5.1.16.0");var subQ2=makeQuery(id+"F0.imprint","INTERSECT",VERTEX,{"disambiguationData":[OD(0.0)],"derivedFrom":[subQ1,subQ0]});Q63=makeQuery(id+"F0.imprint","IMPRINT",FACE,{"disambiguationData":[TD([[makeQuery(id+"F0.imprint","IMPRINT",EDGE,{"disambiguationData":[TD([[subQ2,-1.0]])],"derivedFrom":subQ1}),-1.0]])]});}
            var Q64;
            {var subQ0=sQuery(id+"F0.wireOp",EDGE,"E0");var subQ1=sQuery(id+"F0.wireOp",EDGE,"E5.1.21.0");var subQ2=makeQuery(id+"F0.imprint","INTERSECT",VERTEX,{"disambiguationData":[OD(0.0)],"derivedFrom":[subQ1,subQ0]});Q64=makeQuery(id+"F0.imprint","IMPRINT",FACE,{"disambiguationData":[TD([[makeQuery(id+"F0.imprint","IMPRINT",EDGE,{"disambiguationData":[TD([[subQ2,-1.0]])],"derivedFrom":subQ1}),-1.0]])]});}
            var Q65;
            {var subQ0=sQuery(id+"F0.wireOp",EDGE,"E5.1.23.0");var subQ1=sQuery(id+"F0.wireOp",EDGE,"E5.1.22.0");var subQ2=makeQuery(id+"F0.imprint","INTERSECT",VERTEX,{"disambiguationData":[OD(0.0)],"derivedFrom":[subQ1,subQ0]});Q65=makeQuery(id+"F0.imprint","IMPRINT",FACE,{"disambiguationData":[TD([[makeQuery(id+"F0.imprint","IMPRINT",EDGE,{"disambiguationData":[TD([[subQ2,-1.0]])],"derivedFrom":subQ1}),-1.0]])]});}
            var Q66;
            {var subQ0=sQuery(id+"F0.wireOp",EDGE,"E0");var subQ1=sQuery(id+"F0.wireOp",EDGE,"E5.1.12.0");var subQ2=makeQuery(id+"F0.imprint","INTERSECT",VERTEX,{"disambiguationData":[OD(0.0)],"derivedFrom":[subQ1,subQ0]});Q66=makeQuery(id+"F0.imprint","IMPRINT",FACE,{"disambiguationData":[TD([[makeQuery(id+"F0.imprint","IMPRINT",EDGE,{"disambiguationData":[TD([[subQ2,-1.0]])],"derivedFrom":subQ1}),1.0]])]});}
            var Q67;
            {var subQ0=sQuery(id+"F0.wireOp",EDGE,"E4.1.8.0");var subQ1=sQuery(id+"F0.wireOp",EDGE,"E4.1.7.0");var subQ2=makeQuery(id+"F0.imprint","INTERSECT",VERTEX,{"disambiguationData":[OD(0.0)],"derivedFrom":[subQ1,subQ0]});Q67=makeQuery(id+"F0.imprint","IMPRINT",FACE,{"disambiguationData":[TD([[makeQuery(id+"F0.imprint","IMPRINT",EDGE,{"disambiguationData":[TD([[subQ2,-1.0]])],"derivedFrom":subQ1}),-1.0]])]});}
            var Q68;
            {var subQ0=sQuery(id+"F0.wireOp",EDGE,"E0");var subQ1=sQuery(id+"F0.wireOp",EDGE,"E4.1.6.0");var subQ2=makeQuery(id+"F0.imprint","INTERSECT",VERTEX,{"disambiguationData":[OD(0.0)],"derivedFrom":[subQ1,subQ0]});Q68=makeQuery(id+"F0.imprint","IMPRINT",FACE,{"disambiguationData":[TD([[makeQuery(id+"F0.imprint","IMPRINT",EDGE,{"disambiguationData":[TD([[subQ2,-1.0]])],"derivedFrom":subQ1}),-1.0]])]});}
            var Q69;
            {var subQ0=sQuery(id+"F0.wireOp",EDGE,"E0");var subQ1=sQuery(id+"F0.wireOp",EDGE,"E4.1.3.0");var subQ2=makeQuery(id+"F0.imprint","INTERSECT",VERTEX,{"disambiguationData":[OD(0.0)],"derivedFrom":[subQ1,subQ0]});Q69=makeQuery(id+"F0.imprint","IMPRINT",FACE,{"disambiguationData":[TD([[makeQuery(id+"F0.imprint","IMPRINT",EDGE,{"disambiguationData":[TD([[subQ2,-1.0]])],"derivedFrom":subQ1}),-1.0]])]});}
            var Q70;
            {var subQ0=sQuery(id+"F0.wireOp",EDGE,"E5.1.18.0");var subQ1=sQuery(id+"F0.wireOp",EDGE,"E5.1.17.0");var subQ2=makeQuery(id+"F0.imprint","INTERSECT",VERTEX,{"disambiguationData":[OD(0.0)],"derivedFrom":[subQ1,subQ0]});Q70=makeQuery(id+"F0.imprint","IMPRINT",FACE,{"disambiguationData":[TD([[makeQuery(id+"F0.imprint","IMPRINT",EDGE,{"disambiguationData":[TD([[subQ2,-1.0]])],"derivedFrom":subQ1}),-1.0]])]});}
            var Q71;
            {var subQ0=sQuery(id+"F0.wireOp",EDGE,"E0");var subQ1=sQuery(id+"F0.wireOp",EDGE,"E5.1.26.0");var subQ2=makeQuery(id+"F0.imprint","INTERSECT",VERTEX,{"disambiguationData":[OD(0.0)],"derivedFrom":[subQ1,subQ0]});Q71=makeQuery(id+"F0.imprint","IMPRINT",FACE,{"disambiguationData":[TD([[makeQuery(id+"F0.imprint","IMPRINT",EDGE,{"disambiguationData":[TD([[subQ2,-1.0]])],"derivedFrom":subQ1}),-1.0]])]});}
            var Q72;
            {var subQ0=sQuery(id+"F0.wireOp",EDGE,"E5.1.13.0");var subQ1=sQuery(id+"F0.wireOp",EDGE,"E5.1.12.0");var subQ2=makeQuery(id+"F0.imprint","INTERSECT",VERTEX,{"disambiguationData":[OD(0.0)],"derivedFrom":[subQ1,subQ0]});Q72=makeQuery(id+"F0.imprint","IMPRINT",FACE,{"disambiguationData":[TD([[makeQuery(id+"F0.imprint","IMPRINT",EDGE,{"disambiguationData":[TD([[subQ2,-1.0]])],"derivedFrom":subQ1}),-1.0]])]});}
            var Q73;
            {var subQ0=sQuery(id+"F0.wireOp",EDGE,"E0");var subQ1=sQuery(id+"F0.wireOp",EDGE,"E5.1.16.0");var subQ2=makeQuery(id+"F0.imprint","INTERSECT",VERTEX,{"disambiguationData":[OD(0.0)],"derivedFrom":[subQ1,subQ0]});Q73=makeQuery(id+"F0.imprint","IMPRINT",FACE,{"disambiguationData":[TD([[makeQuery(id+"F0.imprint","IMPRINT",EDGE,{"disambiguationData":[TD([[subQ2,-1.0]])],"derivedFrom":subQ1}),-1.0]])]});}
            var Q74;
            {var subQ0=sQuery(id+"F0.wireOp",EDGE,"E0");var subQ1=sQuery(id+"F0.wireOp",EDGE,"E5.1.19.0");var subQ2=makeQuery(id+"F0.imprint","INTERSECT",VERTEX,{"disambiguationData":[OD(0.0)],"derivedFrom":[subQ1,subQ0]});Q74=makeQuery(id+"F0.imprint","IMPRINT",FACE,{"disambiguationData":[TD([[makeQuery(id+"F0.imprint","IMPRINT",EDGE,{"disambiguationData":[TD([[subQ2,-1.0]])],"derivedFrom":subQ1}),-1.0]])]});}
            var Q75;
            {var subQ0=sQuery(id+"F0.wireOp",EDGE,"E3.2.0");var subQ1=sQuery(id+"F0.wireOp",EDGE,"E3.1.0");var subQ2=makeQuery(id+"F0.imprint","INTERSECT",VERTEX,{"disambiguationData":[OD(0.0)],"derivedFrom":[subQ1,subQ0]});Q75=makeQuery(id+"F0.imprint","IMPRINT",FACE,{"disambiguationData":[TD([[makeQuery(id+"F0.imprint","IMPRINT",EDGE,{"disambiguationData":[TD([[subQ2,-1.0]])],"derivedFrom":subQ1}),-1.0]])]});}
            var Q76;
            {var subQ0=sQuery(id+"F0.wireOp",EDGE,"E5.1.15.0");var subQ1=sQuery(id+"F0.wireOp",EDGE,"E5.1.14.0");var subQ2=makeQuery(id+"F0.imprint","INTERSECT",VERTEX,{"disambiguationData":[OD(0.0)],"derivedFrom":[subQ1,subQ0]});Q76=makeQuery(id+"F0.imprint","IMPRINT",FACE,{"disambiguationData":[TD([[makeQuery(id+"F0.imprint","IMPRINT",EDGE,{"disambiguationData":[TD([[subQ2,-1.0]])],"derivedFrom":subQ1}),-1.0]])]});}
            var Q77;
            {var subQ0=sQuery(id+"F0.wireOp",EDGE,"E5.1.29.0");var subQ1=sQuery(id+"F0.wireOp",EDGE,"E5.1.28.0");var subQ2=makeQuery(id+"F0.imprint","INTERSECT",VERTEX,{"disambiguationData":[OD(0.0)],"derivedFrom":[subQ1,subQ0]});Q77=makeQuery(id+"F0.imprint","IMPRINT",FACE,{"disambiguationData":[TD([[makeQuery(id+"F0.imprint","IMPRINT",EDGE,{"disambiguationData":[TD([[subQ2,-1.0]])],"derivedFrom":subQ1}),-1.0]])]});}
            var Q78;
            {var subQ0=sQuery(id+"F0.wireOp",EDGE,"E0");var subQ1=sQuery(id+"F0.wireOp",EDGE,"E4.1.7.0");var subQ2=makeQuery(id+"F0.imprint","INTERSECT",VERTEX,{"disambiguationData":[OD(0.0)],"derivedFrom":[subQ1,subQ0]});Q78=makeQuery(id+"F0.imprint","IMPRINT",FACE,{"disambiguationData":[TD([[makeQuery(id+"F0.imprint","IMPRINT",EDGE,{"disambiguationData":[TD([[subQ2,-1.0]])],"derivedFrom":subQ1}),-1.0]])]});}
            var Q79;
            {var subQ0=sQuery(id+"F0.wireOp",EDGE,"E5.1.14.0");var subQ1=sQuery(id+"F0.wireOp",EDGE,"E5.1.13.0");var subQ2=makeQuery(id+"F0.imprint","INTERSECT",VERTEX,{"disambiguationData":[OD(0.0)],"derivedFrom":[subQ1,subQ0]});Q79=makeQuery(id+"F0.imprint","IMPRINT",FACE,{"disambiguationData":[TD([[makeQuery(id+"F0.imprint","IMPRINT",EDGE,{"disambiguationData":[TD([[subQ2,-1.0]])],"derivedFrom":subQ1}),1.0]])]});}
            var Q80;
            {var subQ0=sQuery(id+"F0.wireOp",EDGE,"E1");var subQ1=sQuery(id+"F0.wireOp",EDGE,"E7.11.0");var subQ2=makeQuery(id+"F0.imprint","INTERSECT",VERTEX,{"disambiguationData":[OD(0.0)],"derivedFrom":[subQ1,subQ0]});Q80=makeQuery(id+"F0.imprint","IMPRINT",FACE,{"disambiguationData":[TD([[makeQuery(id+"F0.imprint","IMPRINT",EDGE,{"disambiguationData":[TD([[subQ2,-1.0]])],"derivedFrom":subQ1}),1.0]])]});}
            var Q81;
            {var subQ0=sQuery(id+"F0.wireOp",EDGE,"E1");var subQ1=sQuery(id+"F0.wireOp",EDGE,"E8.1.39.0");var subQ2=makeQuery(id+"F0.imprint","INTERSECT",VERTEX,{"disambiguationData":[OD(0.0)],"derivedFrom":[subQ1,subQ0]});Q81=makeQuery(id+"F0.imprint","IMPRINT",FACE,{"disambiguationData":[TD([[makeQuery(id+"F0.imprint","IMPRINT",EDGE,{"disambiguationData":[TD([[subQ2,1.0]])],"derivedFrom":subQ1}),1.0]])]});}
            var Q82;
            {var subQ0=sQuery(id+"F0.wireOp",EDGE,"E1");var subQ1=sQuery(id+"F0.wireOp",EDGE,"E8.1.31.0");var subQ2=makeQuery(id+"F0.imprint","INTERSECT",VERTEX,{"disambiguationData":[OD(0.0)],"derivedFrom":[subQ1,subQ0]});Q82=makeQuery(id+"F0.imprint","IMPRINT",FACE,{"disambiguationData":[TD([[makeQuery(id+"F0.imprint","IMPRINT",EDGE,{"disambiguationData":[TD([[subQ2,1.0]])],"derivedFrom":subQ1}),1.0]])]});}
            var Q83;
            {var subQ0=sQuery(id+"F0.wireOp",EDGE,"E1");var subQ1=sQuery(id+"F0.wireOp",EDGE,"E8.1.28.0");var subQ2=makeQuery(id+"F0.imprint","INTERSECT",VERTEX,{"disambiguationData":[OD(0.0)],"derivedFrom":[subQ1,subQ0]});Q83=makeQuery(id+"F0.imprint","IMPRINT",FACE,{"disambiguationData":[TD([[makeQuery(id+"F0.imprint","IMPRINT",EDGE,{"disambiguationData":[TD([[subQ2,-1.0]])],"derivedFrom":subQ1}),1.0]])]});}
            var Q84;
            {var subQ0=sQuery(id+"F0.wireOp",EDGE,"E1");var subQ1=sQuery(id+"F0.wireOp",EDGE,"E8.1.37.0");var subQ2=makeQuery(id+"F0.imprint","INTERSECT",VERTEX,{"disambiguationData":[OD(0.0)],"derivedFrom":[subQ1,subQ0]});Q84=makeQuery(id+"F0.imprint","IMPRINT",FACE,{"disambiguationData":[TD([[makeQuery(id+"F0.imprint","IMPRINT",EDGE,{"disambiguationData":[TD([[subQ2,-1.0]])],"derivedFrom":subQ1}),1.0]])]});}
            var Q85;
            {var subQ0=sQuery(id+"F0.wireOp",EDGE,"E1");var subQ1=sQuery(id+"F0.wireOp",EDGE,"E8.1.23.0");var subQ2=makeQuery(id+"F0.imprint","INTERSECT",VERTEX,{"disambiguationData":[OD(0.0)],"derivedFrom":[subQ1,subQ0]});Q85=makeQuery(id+"F0.imprint","IMPRINT",FACE,{"disambiguationData":[TD([[makeQuery(id+"F0.imprint","IMPRINT",EDGE,{"disambiguationData":[TD([[subQ2,1.0]])],"derivedFrom":subQ1}),1.0]])]});}
            var Q86;
            {var subQ0=sQuery(id+"F0.wireOp",EDGE,"E0");var subQ1=sQuery(id+"F0.wireOp",EDGE,"E5.1.30.0");var subQ2=makeQuery(id+"F0.imprint","INTERSECT",VERTEX,{"disambiguationData":[OD(0.0)],"derivedFrom":[subQ1,subQ0]});Q86=makeQuery(id+"F0.imprint","IMPRINT",FACE,{"disambiguationData":[TD([[makeQuery(id+"F0.imprint","IMPRINT",EDGE,{"disambiguationData":[TD([[subQ2,-1.0]])],"derivedFrom":subQ1}),1.0]])]});}
            var Q87;
            {var subQ0=sQuery(id+"F0.wireOp",EDGE,"E1");var subQ1=sQuery(id+"F0.wireOp",EDGE,"E7.15.0");var subQ2=makeQuery(id+"F0.imprint","INTERSECT",VERTEX,{"disambiguationData":[OD(0.0)],"derivedFrom":[subQ1,subQ0]});Q87=makeQuery(id+"F0.imprint","IMPRINT",FACE,{"disambiguationData":[TD([[makeQuery(id+"F0.imprint","IMPRINT",EDGE,{"disambiguationData":[TD([[subQ2,1.0]])],"derivedFrom":subQ1}),1.0]])]});}
            var Q88;
            {var subQ0=sQuery(id+"F0.wireOp",EDGE,"E1");var subQ1=sQuery(id+"F0.wireOp",EDGE,"E7.9.0");var subQ2=makeQuery(id+"F0.imprint","INTERSECT",VERTEX,{"disambiguationData":[OD(0.0)],"derivedFrom":[subQ1,subQ0]});Q88=makeQuery(id+"F0.imprint","IMPRINT",FACE,{"disambiguationData":[TD([[makeQuery(id+"F0.imprint","IMPRINT",EDGE,{"disambiguationData":[TD([[subQ2,1.0]])],"derivedFrom":subQ1}),1.0]])]});}
            var Q89;
            {var subQ0=sQuery(id+"F0.wireOp",EDGE,"E1");var subQ1=sQuery(id+"F0.wireOp",EDGE,"E8.1.32.0");var subQ2=makeQuery(id+"F0.imprint","INTERSECT",VERTEX,{"disambiguationData":[OD(0.0)],"derivedFrom":[subQ1,subQ0]});Q89=makeQuery(id+"F0.imprint","IMPRINT",FACE,{"disambiguationData":[TD([[makeQuery(id+"F0.imprint","IMPRINT",EDGE,{"disambiguationData":[TD([[subQ2,-1.0]])],"derivedFrom":subQ1}),1.0]])]});}
            var Q90;
            {var subQ0=sQuery(id+"F0.wireOp",EDGE,"E0");var subQ1=sQuery(id+"F0.wireOp",EDGE,"E2");var subQ2=makeQuery(id+"F0.imprint","INTERSECT",VERTEX,{"disambiguationData":[OD(0.0)],"derivedFrom":[subQ1,subQ0]});Q90=makeQuery(id+"F0.imprint","IMPRINT",FACE,{"disambiguationData":[TD([[makeQuery(id+"F0.imprint","IMPRINT",EDGE,{"disambiguationData":[TD([[subQ2,-1.0]])],"derivedFrom":subQ1}),1.0]])]});}
            var Q91;
            {var subQ0=sQuery(id+"F0.wireOp",EDGE,"E0");var subQ1=sQuery(id+"F0.wireOp",EDGE,"E5.1.11.0");var subQ2=makeQuery(id+"F0.imprint","INTERSECT",VERTEX,{"disambiguationData":[OD(0.0)],"derivedFrom":[subQ1,subQ0]});Q91=makeQuery(id+"F0.imprint","IMPRINT",FACE,{"disambiguationData":[TD([[makeQuery(id+"F0.imprint","IMPRINT",EDGE,{"disambiguationData":[TD([[subQ2,-1.0]])],"derivedFrom":subQ1}),1.0]])]});}
            var Q92;
            {var subQ0=sQuery(id+"F0.wireOp",EDGE,"E1");var subQ1=sQuery(id+"F0.wireOp",EDGE,"E7.19.0");var subQ2=makeQuery(id+"F0.imprint","INTERSECT",VERTEX,{"disambiguationData":[OD(0.0)],"derivedFrom":[subQ1,subQ0]});Q92=makeQuery(id+"F0.imprint","IMPRINT",FACE,{"disambiguationData":[TD([[makeQuery(id+"F0.imprint","IMPRINT",EDGE,{"disambiguationData":[TD([[subQ2,-1.0]])],"derivedFrom":subQ1}),1.0]])]});}
            var Q93;
            {var subQ0=sQuery(id+"F0.wireOp",EDGE,"E1");var subQ1=sQuery(id+"F0.wireOp",EDGE,"E8.1.24.0");var subQ2=makeQuery(id+"F0.imprint","INTERSECT",VERTEX,{"disambiguationData":[OD(0.0)],"derivedFrom":[subQ1,subQ0]});Q93=makeQuery(id+"F0.imprint","IMPRINT",FACE,{"disambiguationData":[TD([[makeQuery(id+"F0.imprint","IMPRINT",EDGE,{"disambiguationData":[TD([[subQ2,-1.0]])],"derivedFrom":subQ1}),1.0]])]});}
            var Q94;
            {var subQ0=sQuery(id+"F0.wireOp",EDGE,"E1");var subQ1=sQuery(id+"F0.wireOp",EDGE,"E7.15.0");var subQ2=makeQuery(id+"F0.imprint","INTERSECT",VERTEX,{"disambiguationData":[OD(0.0)],"derivedFrom":[subQ1,subQ0]});Q94=makeQuery(id+"F0.imprint","IMPRINT",FACE,{"disambiguationData":[TD([[makeQuery(id+"F0.imprint","IMPRINT",EDGE,{"disambiguationData":[TD([[subQ2,-1.0]])],"derivedFrom":subQ1}),1.0]])]});}
            var Q95;
            {var subQ0=sQuery(id+"F0.wireOp",EDGE,"E1");var subQ1=sQuery(id+"F0.wireOp",EDGE,"E7.13.0");var subQ2=makeQuery(id+"F0.imprint","INTERSECT",VERTEX,{"disambiguationData":[OD(0.0)],"derivedFrom":[subQ1,subQ0]});Q95=makeQuery(id+"F0.imprint","IMPRINT",FACE,{"disambiguationData":[TD([[makeQuery(id+"F0.imprint","IMPRINT",EDGE,{"disambiguationData":[TD([[subQ2,-1.0]])],"derivedFrom":subQ1}),1.0]])]});}
            var Q96;
            {var subQ0=sQuery(id+"F0.wireOp",EDGE,"E1");var subQ1=sQuery(id+"F0.wireOp",EDGE,"E8.1.22.0");var subQ2=makeQuery(id+"F0.imprint","INTERSECT",VERTEX,{"disambiguationData":[OD(0.0)],"derivedFrom":[subQ1,subQ0]});Q96=makeQuery(id+"F0.imprint","IMPRINT",FACE,{"disambiguationData":[TD([[makeQuery(id+"F0.imprint","IMPRINT",EDGE,{"disambiguationData":[TD([[subQ2,-1.0]])],"derivedFrom":subQ1}),1.0]])]});}
            var Q97;
            {var subQ0=sQuery(id+"F0.wireOp",EDGE,"E1");var subQ1=sQuery(id+"F0.wireOp",EDGE,"E8.1.29.0");var subQ2=makeQuery(id+"F0.imprint","INTERSECT",VERTEX,{"disambiguationData":[OD(0.0)],"derivedFrom":[subQ1,subQ0]});Q97=makeQuery(id+"F0.imprint","IMPRINT",FACE,{"disambiguationData":[TD([[makeQuery(id+"F0.imprint","IMPRINT",EDGE,{"disambiguationData":[TD([[subQ2,-1.0]])],"derivedFrom":subQ1}),1.0]])]});}
            var Q98;
            {var subQ0=sQuery(id+"F0.wireOp",EDGE,"E1");var subQ1=sQuery(id+"F0.wireOp",EDGE,"E8.1.30.0");var subQ2=makeQuery(id+"F0.imprint","INTERSECT",VERTEX,{"disambiguationData":[OD(0.0)],"derivedFrom":[subQ1,subQ0]});Q98=makeQuery(id+"F0.imprint","IMPRINT",FACE,{"disambiguationData":[TD([[makeQuery(id+"F0.imprint","IMPRINT",EDGE,{"disambiguationData":[TD([[subQ2,-1.0]])],"derivedFrom":subQ1}),1.0]])]});}
            var Q99;
            {var subQ0=sQuery(id+"F0.wireOp",EDGE,"E1");var subQ1=sQuery(id+"F0.wireOp",EDGE,"E8.1.38.0");var subQ2=makeQuery(id+"F0.imprint","INTERSECT",VERTEX,{"disambiguationData":[OD(0.0)],"derivedFrom":[subQ1,subQ0]});Q99=makeQuery(id+"F0.imprint","IMPRINT",FACE,{"disambiguationData":[TD([[makeQuery(id+"F0.imprint","IMPRINT",EDGE,{"disambiguationData":[TD([[subQ2,-1.0]])],"derivedFrom":subQ1}),1.0]])]});}
            var Q100;
            {var subQ0=sQuery(id+"F0.wireOp",EDGE,"E1");var subQ1=sQuery(id+"F0.wireOp",EDGE,"E8.1.37.0");var subQ2=makeQuery(id+"F0.imprint","INTERSECT",VERTEX,{"disambiguationData":[OD(0.0)],"derivedFrom":[subQ1,subQ0]});Q100=makeQuery(id+"F0.imprint","IMPRINT",FACE,{"disambiguationData":[TD([[makeQuery(id+"F0.imprint","IMPRINT",EDGE,{"disambiguationData":[TD([[subQ2,1.0]])],"derivedFrom":subQ1}),1.0]])]});}
            var Q101;
            {var subQ0=sQuery(id+"F0.wireOp",EDGE,"E1");var subQ1=sQuery(id+"F0.wireOp",EDGE,"E8.1.21.0");var subQ2=makeQuery(id+"F0.imprint","INTERSECT",VERTEX,{"disambiguationData":[OD(0.0)],"derivedFrom":[subQ1,subQ0]});Q101=makeQuery(id+"F0.imprint","IMPRINT",FACE,{"disambiguationData":[TD([[makeQuery(id+"F0.imprint","IMPRINT",EDGE,{"disambiguationData":[TD([[subQ2,-1.0]])],"derivedFrom":subQ1}),1.0]])]});}
            var Q102;
            {var subQ0=sQuery(id+"F0.wireOp",EDGE,"E5.1.16.0");var subQ1=sQuery(id+"F0.wireOp",EDGE,"E5.1.15.0");var subQ2=makeQuery(id+"F0.imprint","INTERSECT",VERTEX,{"disambiguationData":[OD(0.0)],"derivedFrom":[subQ1,subQ0]});Q102=makeQuery(id+"F0.imprint","IMPRINT",FACE,{"disambiguationData":[TD([[makeQuery(id+"F0.imprint","IMPRINT",EDGE,{"disambiguationData":[TD([[subQ2,-1.0]])],"derivedFrom":subQ1}),1.0]])]});}
            var Q103;
            {var subQ0=sQuery(id+"F0.wireOp",EDGE,"E0");var subQ1=sQuery(id+"F0.wireOp",EDGE,"E4.1.9.0");var subQ2=makeQuery(id+"F0.imprint","INTERSECT",VERTEX,{"disambiguationData":[OD(0.0)],"derivedFrom":[subQ1,subQ0]});Q103=makeQuery(id+"F0.imprint","IMPRINT",FACE,{"disambiguationData":[TD([[makeQuery(id+"F0.imprint","IMPRINT",EDGE,{"disambiguationData":[TD([[subQ2,-1.0]])],"derivedFrom":subQ1}),1.0]])]});}
            var Q104;
            {var subQ0=sQuery(id+"F0.wireOp",EDGE,"E1");var subQ1=sQuery(id+"F0.wireOp",EDGE,"E7.16.0");var subQ2=makeQuery(id+"F0.imprint","INTERSECT",VERTEX,{"disambiguationData":[OD(0.0)],"derivedFrom":[subQ1,subQ0]});Q104=makeQuery(id+"F0.imprint","IMPRINT",FACE,{"disambiguationData":[TD([[makeQuery(id+"F0.imprint","IMPRINT",EDGE,{"disambiguationData":[TD([[subQ2,-1.0]])],"derivedFrom":subQ1}),1.0]])]});}
            var Q105;
            {var subQ0=sQuery(id+"F0.wireOp",EDGE,"E1");var subQ1=sQuery(id+"F0.wireOp",EDGE,"E7.8.0");var subQ2=makeQuery(id+"F0.imprint","INTERSECT",VERTEX,{"disambiguationData":[OD(0.0)],"derivedFrom":[subQ1,subQ0]});Q105=makeQuery(id+"F0.imprint","IMPRINT",FACE,{"disambiguationData":[TD([[makeQuery(id+"F0.imprint","IMPRINT",EDGE,{"disambiguationData":[TD([[subQ2,-1.0]])],"derivedFrom":subQ1}),1.0]])]});}
            var Q106;
            {var subQ0=sQuery(id+"F0.wireOp",EDGE,"E1");var subQ1=sQuery(id+"F0.wireOp",EDGE,"E8.1.33.0");var subQ2=makeQuery(id+"F0.imprint","INTERSECT",VERTEX,{"disambiguationData":[OD(0.0)],"derivedFrom":[subQ1,subQ0]});Q106=makeQuery(id+"F0.imprint","IMPRINT",FACE,{"disambiguationData":[TD([[makeQuery(id+"F0.imprint","IMPRINT",EDGE,{"disambiguationData":[TD([[subQ2,1.0]])],"derivedFrom":subQ1}),1.0]])]});}
            var Q107;
            {var subQ0=sQuery(id+"F0.wireOp",EDGE,"E1");var subQ1=sQuery(id+"F0.wireOp",EDGE,"E8.1.25.0");var subQ2=makeQuery(id+"F0.imprint","INTERSECT",VERTEX,{"disambiguationData":[OD(0.0)],"derivedFrom":[subQ1,subQ0]});Q107=makeQuery(id+"F0.imprint","IMPRINT",FACE,{"disambiguationData":[TD([[makeQuery(id+"F0.imprint","IMPRINT",EDGE,{"disambiguationData":[TD([[subQ2,1.0]])],"derivedFrom":subQ1}),1.0]])]});}
            var Q108;
            {var subQ0=sQuery(id+"F0.wireOp",EDGE,"E1");var subQ1=sQuery(id+"F0.wireOp",EDGE,"E7.17.0");var subQ2=makeQuery(id+"F0.imprint","INTERSECT",VERTEX,{"disambiguationData":[OD(0.0)],"derivedFrom":[subQ1,subQ0]});Q108=makeQuery(id+"F0.imprint","IMPRINT",FACE,{"disambiguationData":[TD([[makeQuery(id+"F0.imprint","IMPRINT",EDGE,{"disambiguationData":[TD([[subQ2,1.0]])],"derivedFrom":subQ1}),1.0]])]});}
            var Q109;
            {var subQ0=sQuery(id+"F0.wireOp",EDGE,"E1");var subQ1=sQuery(id+"F0.wireOp",EDGE,"E7.9.0");var subQ2=makeQuery(id+"F0.imprint","INTERSECT",VERTEX,{"disambiguationData":[OD(0.0)],"derivedFrom":[subQ1,subQ0]});Q109=makeQuery(id+"F0.imprint","IMPRINT",FACE,{"disambiguationData":[TD([[makeQuery(id+"F0.imprint","IMPRINT",EDGE,{"disambiguationData":[TD([[subQ2,-1.0]])],"derivedFrom":subQ1}),1.0]])]});}
            var Q110;
            {var subQ0=sQuery(id+"F0.wireOp",EDGE,"E5.1.31.0");var subQ1=sQuery(id+"F0.wireOp",EDGE,"E2");var subQ2=makeQuery(id+"F0.imprint","INTERSECT",VERTEX,{"disambiguationData":[OD(1.0)],"derivedFrom":[subQ1,subQ0]});Q110=makeQuery(id+"F0.imprint","IMPRINT",FACE,{"disambiguationData":[TD([[makeQuery(id+"F0.imprint","IMPRINT",EDGE,{"disambiguationData":[TD([[subQ2,-1.0]])],"derivedFrom":subQ1}),1.0]])]});}
            var Q111;
            {var subQ0=sQuery(id+"F0.wireOp",EDGE,"E1");var subQ1=sQuery(id+"F0.wireOp",EDGE,"E8.1.25.0");var subQ2=makeQuery(id+"F0.imprint","INTERSECT",VERTEX,{"disambiguationData":[OD(0.0)],"derivedFrom":[subQ1,subQ0]});Q111=makeQuery(id+"F0.imprint","IMPRINT",FACE,{"disambiguationData":[TD([[makeQuery(id+"F0.imprint","IMPRINT",EDGE,{"disambiguationData":[TD([[subQ2,-1.0]])],"derivedFrom":subQ1}),1.0]])]});}
            var Q112;
            {var subQ0=sQuery(id+"F0.wireOp",EDGE,"E1");var subQ1=sQuery(id+"F0.wireOp",EDGE,"E7.17.0");var subQ2=makeQuery(id+"F0.imprint","INTERSECT",VERTEX,{"disambiguationData":[OD(0.0)],"derivedFrom":[subQ1,subQ0]});Q112=makeQuery(id+"F0.imprint","IMPRINT",FACE,{"disambiguationData":[TD([[makeQuery(id+"F0.imprint","IMPRINT",EDGE,{"disambiguationData":[TD([[subQ2,-1.0]])],"derivedFrom":subQ1}),1.0]])]});}
            var Q113;
            {var subQ0=sQuery(id+"F0.wireOp",EDGE,"E0");var subQ1=sQuery(id+"F0.wireOp",EDGE,"E5.1.15.0");var subQ2=makeQuery(id+"F0.imprint","INTERSECT",VERTEX,{"disambiguationData":[OD(0.0)],"derivedFrom":[subQ1,subQ0]});Q113=makeQuery(id+"F0.imprint","IMPRINT",FACE,{"disambiguationData":[TD([[makeQuery(id+"F0.imprint","IMPRINT",EDGE,{"disambiguationData":[TD([[subQ2,-1.0]])],"derivedFrom":subQ1}),1.0]])]});}
            var Q114;
            {var subQ0=sQuery(id+"F0.wireOp",EDGE,"E1");var subQ1=sQuery(id+"F0.wireOp",EDGE,"E8.1.30.0");var subQ2=makeQuery(id+"F0.imprint","INTERSECT",VERTEX,{"disambiguationData":[OD(0.0)],"derivedFrom":[subQ1,subQ0]});Q114=makeQuery(id+"F0.imprint","IMPRINT",FACE,{"disambiguationData":[TD([[makeQuery(id+"F0.imprint","IMPRINT",EDGE,{"disambiguationData":[TD([[subQ2,1.0]])],"derivedFrom":subQ1}),1.0]])]});}
            var Q115;
            {var subQ0=sQuery(id+"F0.wireOp",EDGE,"E1");var subQ1=sQuery(id+"F0.wireOp",EDGE,"E8.1.22.0");var subQ2=makeQuery(id+"F0.imprint","INTERSECT",VERTEX,{"disambiguationData":[OD(0.0)],"derivedFrom":[subQ1,subQ0]});Q115=makeQuery(id+"F0.imprint","IMPRINT",FACE,{"disambiguationData":[TD([[makeQuery(id+"F0.imprint","IMPRINT",EDGE,{"disambiguationData":[TD([[subQ2,1.0]])],"derivedFrom":subQ1}),1.0]])]});}
            var Q116;
            {var subQ0=sQuery(id+"F0.wireOp",EDGE,"E1");var subQ1=sQuery(id+"F0.wireOp",EDGE,"E7.10.0");var subQ2=makeQuery(id+"F0.imprint","INTERSECT",VERTEX,{"disambiguationData":[OD(0.0)],"derivedFrom":[subQ1,subQ0]});Q116=makeQuery(id+"F0.imprint","IMPRINT",FACE,{"disambiguationData":[TD([[makeQuery(id+"F0.imprint","IMPRINT",EDGE,{"disambiguationData":[TD([[subQ2,1.0]])],"derivedFrom":subQ1}),1.0]])]});}
            var Q117;
            {var subQ0=sQuery(id+"F0.wireOp",EDGE,"E1");var subQ1=sQuery(id+"F0.wireOp",EDGE,"E7.8.0");var subQ2=makeQuery(id+"F0.imprint","INTERSECT",VERTEX,{"disambiguationData":[OD(0.0)],"derivedFrom":[subQ1,subQ0]});Q117=makeQuery(id+"F0.imprint","IMPRINT",FACE,{"disambiguationData":[TD([[makeQuery(id+"F0.imprint","IMPRINT",EDGE,{"disambiguationData":[TD([[subQ2,1.0]])],"derivedFrom":subQ1}),1.0]])]});}
            var Q118;
            {var subQ0=sQuery(id+"F0.wireOp",EDGE,"E1");var subQ1=sQuery(id+"F0.wireOp",EDGE,"E8.1.34.0");var subQ2=makeQuery(id+"F0.imprint","INTERSECT",VERTEX,{"disambiguationData":[OD(0.0)],"derivedFrom":[subQ1,subQ0]});Q118=makeQuery(id+"F0.imprint","IMPRINT",FACE,{"disambiguationData":[TD([[makeQuery(id+"F0.imprint","IMPRINT",EDGE,{"disambiguationData":[TD([[subQ2,-1.0]])],"derivedFrom":subQ1}),1.0]])]});}
            var Q119;
            {var subQ0=sQuery(id+"F0.wireOp",EDGE,"E1");var subQ1=sQuery(id+"F0.wireOp",EDGE,"E8.1.26.0");var subQ2=makeQuery(id+"F0.imprint","INTERSECT",VERTEX,{"disambiguationData":[OD(0.0)],"derivedFrom":[subQ1,subQ0]});Q119=makeQuery(id+"F0.imprint","IMPRINT",FACE,{"disambiguationData":[TD([[makeQuery(id+"F0.imprint","IMPRINT",EDGE,{"disambiguationData":[TD([[subQ2,1.0]])],"derivedFrom":subQ1}),1.0]])]});}
            var Q120;
            {var subQ0=sQuery(id+"F0.wireOp",EDGE,"E1");var subQ1=sQuery(id+"F0.wireOp",EDGE,"E7.6.0");var subQ2=makeQuery(id+"F0.imprint","INTERSECT",VERTEX,{"disambiguationData":[OD(0.0)],"derivedFrom":[subQ1,subQ0]});Q120=makeQuery(id+"F0.imprint","IMPRINT",FACE,{"disambiguationData":[TD([[makeQuery(id+"F0.imprint","IMPRINT",EDGE,{"disambiguationData":[TD([[subQ2,-1.0]])],"derivedFrom":subQ1}),1.0]])]});}
            var Q121;
            {var subQ0=sQuery(id+"F0.wireOp",EDGE,"E0");var subQ1=sQuery(id+"F0.wireOp",EDGE,"E5.1.10.0");var subQ2=makeQuery(id+"F0.imprint","INTERSECT",VERTEX,{"disambiguationData":[OD(0.0)],"derivedFrom":[subQ1,subQ0]});Q121=makeQuery(id+"F0.imprint","IMPRINT",FACE,{"disambiguationData":[TD([[makeQuery(id+"F0.imprint","IMPRINT",EDGE,{"disambiguationData":[TD([[subQ2,-1.0]])],"derivedFrom":subQ1}),1.0]])]});}
            var Q122;
            {var subQ0=sQuery(id+"F0.wireOp",EDGE,"E0");var subQ1=sQuery(id+"F0.wireOp",EDGE,"E5.1.26.0");var subQ2=makeQuery(id+"F0.imprint","INTERSECT",VERTEX,{"disambiguationData":[OD(0.0)],"derivedFrom":[subQ1,subQ0]});Q122=makeQuery(id+"F0.imprint","IMPRINT",FACE,{"disambiguationData":[TD([[makeQuery(id+"F0.imprint","IMPRINT",EDGE,{"disambiguationData":[TD([[subQ2,-1.0]])],"derivedFrom":subQ1}),1.0]])]});}
            var Q123;
            {var subQ0=sQuery(id+"F0.wireOp",EDGE,"E1");var subQ1=sQuery(id+"F0.wireOp",EDGE,"E7.7.0");var subQ2=makeQuery(id+"F0.imprint","INTERSECT",VERTEX,{"disambiguationData":[OD(0.0)],"derivedFrom":[subQ1,subQ0]});Q123=makeQuery(id+"F0.imprint","IMPRINT",FACE,{"disambiguationData":[TD([[makeQuery(id+"F0.imprint","IMPRINT",EDGE,{"disambiguationData":[TD([[subQ2,-1.0]])],"derivedFrom":subQ1}),1.0]])]});}
            var Q124;
            {var subQ0=sQuery(id+"F0.wireOp",EDGE,"E1");var subQ1=sQuery(id+"F0.wireOp",EDGE,"E7.11.0");var subQ2=makeQuery(id+"F0.imprint","INTERSECT",VERTEX,{"disambiguationData":[OD(0.0)],"derivedFrom":[subQ1,subQ0]});Q124=makeQuery(id+"F0.imprint","IMPRINT",FACE,{"disambiguationData":[TD([[makeQuery(id+"F0.imprint","IMPRINT",EDGE,{"disambiguationData":[TD([[subQ2,1.0]])],"derivedFrom":subQ1}),1.0]])]});}
            var Q125;
            {var subQ0=sQuery(id+"F0.wireOp",EDGE,"E1");var subQ1=sQuery(id+"F0.wireOp",EDGE,"E7.19.0");var subQ2=makeQuery(id+"F0.imprint","INTERSECT",VERTEX,{"disambiguationData":[OD(0.0)],"derivedFrom":[subQ1,subQ0]});Q125=makeQuery(id+"F0.imprint","IMPRINT",FACE,{"disambiguationData":[TD([[makeQuery(id+"F0.imprint","IMPRINT",EDGE,{"disambiguationData":[TD([[subQ2,1.0]])],"derivedFrom":subQ1}),1.0]])]});}
            var Q126;
            {var subQ0=sQuery(id+"F0.wireOp",EDGE,"E1");var subQ1=sQuery(id+"F0.wireOp",EDGE,"E8.1.35.0");var subQ2=makeQuery(id+"F0.imprint","INTERSECT",VERTEX,{"disambiguationData":[OD(0.0)],"derivedFrom":[subQ1,subQ0]});Q126=makeQuery(id+"F0.imprint","IMPRINT",FACE,{"disambiguationData":[TD([[makeQuery(id+"F0.imprint","IMPRINT",EDGE,{"disambiguationData":[TD([[subQ2,1.0]])],"derivedFrom":subQ1}),1.0]])]});}
            var Q127;
            {var subQ0=sQuery(id+"F0.wireOp",EDGE,"E4.1.7.0");var subQ1=sQuery(id+"F0.wireOp",EDGE,"E4.1.6.0");var subQ2=makeQuery(id+"F0.imprint","INTERSECT",VERTEX,{"disambiguationData":[OD(0.0)],"derivedFrom":[subQ1,subQ0]});Q127=makeQuery(id+"F0.imprint","IMPRINT",FACE,{"disambiguationData":[TD([[makeQuery(id+"F0.imprint","IMPRINT",EDGE,{"disambiguationData":[TD([[subQ2,-1.0]])],"derivedFrom":subQ1}),1.0]])]});}
            var Q128;
            {var subQ0=sQuery(id+"F0.wireOp",EDGE,"E1");var subQ1=sQuery(id+"F0.wireOp",EDGE,"E8.1.32.0");var subQ2=makeQuery(id+"F0.imprint","INTERSECT",VERTEX,{"disambiguationData":[OD(0.0)],"derivedFrom":[subQ1,subQ0]});Q128=makeQuery(id+"F0.imprint","IMPRINT",FACE,{"disambiguationData":[TD([[makeQuery(id+"F0.imprint","IMPRINT",EDGE,{"disambiguationData":[TD([[subQ2,1.0]])],"derivedFrom":subQ1}),1.0]])]});}
            var Q129;
            {var subQ0=sQuery(id+"F0.wireOp",EDGE,"E1");var subQ1=sQuery(id+"F0.wireOp",EDGE,"E7.10.0");var subQ2=makeQuery(id+"F0.imprint","INTERSECT",VERTEX,{"disambiguationData":[OD(0.0)],"derivedFrom":[subQ1,subQ0]});Q129=makeQuery(id+"F0.imprint","IMPRINT",FACE,{"disambiguationData":[TD([[makeQuery(id+"F0.imprint","IMPRINT",EDGE,{"disambiguationData":[TD([[subQ2,-1.0]])],"derivedFrom":subQ1}),1.0]])]});}
            var Q130;
            {var subQ0=sQuery(id+"F0.wireOp",EDGE,"E1");var subQ1=sQuery(id+"F0.wireOp",EDGE,"E8.1.26.0");var subQ2=makeQuery(id+"F0.imprint","INTERSECT",VERTEX,{"disambiguationData":[OD(0.0)],"derivedFrom":[subQ1,subQ0]});Q130=makeQuery(id+"F0.imprint","IMPRINT",FACE,{"disambiguationData":[TD([[makeQuery(id+"F0.imprint","IMPRINT",EDGE,{"disambiguationData":[TD([[subQ2,-1.0]])],"derivedFrom":subQ1}),1.0]])]});}
            var Q131;
            {var subQ0=sQuery(id+"F0.wireOp",EDGE,"E1");var subQ1=sQuery(id+"F0.wireOp",EDGE,"E7.18.0");var subQ2=makeQuery(id+"F0.imprint","INTERSECT",VERTEX,{"disambiguationData":[OD(0.0)],"derivedFrom":[subQ1,subQ0]});Q131=makeQuery(id+"F0.imprint","IMPRINT",FACE,{"disambiguationData":[TD([[makeQuery(id+"F0.imprint","IMPRINT",EDGE,{"disambiguationData":[TD([[subQ2,-1.0]])],"derivedFrom":subQ1}),1.0]])]});}
            var Q132;
            {var subQ0=sQuery(id+"F0.wireOp",EDGE,"E1");var subQ1=sQuery(id+"F0.wireOp",EDGE,"E8.1.27.0");var subQ2=makeQuery(id+"F0.imprint","INTERSECT",VERTEX,{"disambiguationData":[OD(0.0)],"derivedFrom":[subQ1,subQ0]});Q132=makeQuery(id+"F0.imprint","IMPRINT",FACE,{"disambiguationData":[TD([[makeQuery(id+"F0.imprint","IMPRINT",EDGE,{"disambiguationData":[TD([[subQ2,-1.0]])],"derivedFrom":subQ1}),1.0]])]});}
            var Q133;
            {var subQ0=sQuery(id+"F0.wireOp",EDGE,"E1");var subQ1=sQuery(id+"F0.wireOp",EDGE,"E7.5.0");var subQ2=makeQuery(id+"F0.imprint","INTERSECT",VERTEX,{"disambiguationData":[OD(0.0)],"derivedFrom":[subQ1,subQ0]});Q133=makeQuery(id+"F0.imprint","IMPRINT",FACE,{"disambiguationData":[TD([[makeQuery(id+"F0.imprint","IMPRINT",EDGE,{"disambiguationData":[TD([[subQ2,1.0]])],"derivedFrom":subQ1}),1.0]])]});}
            var Q134;
            {var subQ0=sQuery(id+"F0.wireOp",EDGE,"E1");var subQ1=sQuery(id+"F0.wireOp",EDGE,"E7.3.0");var subQ2=makeQuery(id+"F0.imprint","INTERSECT",VERTEX,{"disambiguationData":[OD(0.0)],"derivedFrom":[subQ1,subQ0]});Q134=makeQuery(id+"F0.imprint","IMPRINT",FACE,{"disambiguationData":[TD([[makeQuery(id+"F0.imprint","IMPRINT",EDGE,{"disambiguationData":[TD([[subQ2,-1.0]])],"derivedFrom":subQ1}),1.0]])]});}
            var Q135;
            {var subQ0=sQuery(id+"F0.wireOp",EDGE,"E1");var subQ1=sQuery(id+"F0.wireOp",EDGE,"E7.3.0");var subQ2=makeQuery(id+"F0.imprint","INTERSECT",VERTEX,{"disambiguationData":[OD(0.0)],"derivedFrom":[subQ1,subQ0]});Q135=makeQuery(id+"F0.imprint","IMPRINT",FACE,{"disambiguationData":[TD([[makeQuery(id+"F0.imprint","IMPRINT",EDGE,{"disambiguationData":[TD([[subQ2,1.0]])],"derivedFrom":subQ1}),1.0]])]});}
            var Q136;
            {var subQ0=sQuery(id+"F0.wireOp",EDGE,"E0");var subQ1=sQuery(id+"F0.wireOp",EDGE,"E5.1.27.0");var subQ2=makeQuery(id+"F0.imprint","INTERSECT",VERTEX,{"disambiguationData":[OD(0.0)],"derivedFrom":[subQ1,subQ0]});Q136=makeQuery(id+"F0.imprint","IMPRINT",FACE,{"disambiguationData":[TD([[makeQuery(id+"F0.imprint","IMPRINT",EDGE,{"disambiguationData":[TD([[subQ2,-1.0]])],"derivedFrom":subQ1}),1.0]])]});}
            var Q137;
            {var subQ0=sQuery(id+"F0.wireOp",EDGE,"E1");var subQ1=sQuery(id+"F0.wireOp",EDGE,"E7.1.0");var subQ2=makeQuery(id+"F0.imprint","INTERSECT",VERTEX,{"disambiguationData":[OD(0.0)],"derivedFrom":[subQ1,subQ0]});Q137=makeQuery(id+"F0.imprint","IMPRINT",FACE,{"disambiguationData":[TD([[makeQuery(id+"F0.imprint","IMPRINT",EDGE,{"disambiguationData":[TD([[subQ2,-1.0]])],"derivedFrom":subQ1}),1.0]])]});}
            var Q138;
            {var subQ0=sQuery(id+"F0.wireOp",EDGE,"E1");var subQ1=sQuery(id+"F0.wireOp",EDGE,"E7.1.0");var subQ2=makeQuery(id+"F0.imprint","INTERSECT",VERTEX,{"disambiguationData":[OD(0.0)],"derivedFrom":[subQ1,subQ0]});Q138=makeQuery(id+"F0.imprint","IMPRINT",FACE,{"disambiguationData":[TD([[makeQuery(id+"F0.imprint","IMPRINT",EDGE,{"disambiguationData":[TD([[subQ2,1.0]])],"derivedFrom":subQ1}),1.0]])]});}
            var Q139;
            {var subQ0=sQuery(id+"F0.wireOp",EDGE,"E1");var subQ1=sQuery(id+"F0.wireOp",EDGE,"E6");var subQ2=makeQuery(id+"F0.imprint","INTERSECT",VERTEX,{"disambiguationData":[OD(0.0)],"derivedFrom":[subQ1,subQ0]});Q139=makeQuery(id+"F0.imprint","IMPRINT",FACE,{"disambiguationData":[TD([[makeQuery(id+"F0.imprint","IMPRINT",EDGE,{"disambiguationData":[TD([[subQ2,-1.0]])],"derivedFrom":subQ1}),1.0]])]});}
            var Q140;
            {var subQ0=sQuery(id+"F0.wireOp",EDGE,"E1");var subQ1=sQuery(id+"F0.wireOp",EDGE,"E6");var subQ2=makeQuery(id+"F0.imprint","INTERSECT",VERTEX,{"disambiguationData":[OD(0.0)],"derivedFrom":[subQ1,subQ0]});Q140=makeQuery(id+"F0.imprint","IMPRINT",FACE,{"disambiguationData":[TD([[makeQuery(id+"F0.imprint","IMPRINT",EDGE,{"disambiguationData":[TD([[subQ2,1.0]])],"derivedFrom":subQ1}),1.0]])]});}
            var Q141;
            {var subQ0=sQuery(id+"F0.wireOp",EDGE,"E1");var subQ1=sQuery(id+"F0.wireOp",EDGE,"E8.1.24.0");var subQ2=makeQuery(id+"F0.imprint","INTERSECT",VERTEX,{"disambiguationData":[OD(0.0)],"derivedFrom":[subQ1,subQ0]});Q141=makeQuery(id+"F0.imprint","IMPRINT",FACE,{"disambiguationData":[TD([[makeQuery(id+"F0.imprint","IMPRINT",EDGE,{"disambiguationData":[TD([[subQ2,1.0]])],"derivedFrom":subQ1}),1.0]])]});}
            var Q142;
            {var subQ0=sQuery(id+"F0.wireOp",EDGE,"E1");var subQ1=sQuery(id+"F0.wireOp",EDGE,"E8.1.29.0");var subQ2=makeQuery(id+"F0.imprint","INTERSECT",VERTEX,{"disambiguationData":[OD(0.0)],"derivedFrom":[subQ1,subQ0]});Q142=makeQuery(id+"F0.imprint","IMPRINT",FACE,{"disambiguationData":[TD([[makeQuery(id+"F0.imprint","IMPRINT",EDGE,{"disambiguationData":[TD([[subQ2,1.0]])],"derivedFrom":subQ1}),1.0]])]});}
            var Q143;
            {var subQ0=sQuery(id+"F0.wireOp",EDGE,"E1");var subQ1=sQuery(id+"F0.wireOp",EDGE,"E8.1.21.0");var subQ2=makeQuery(id+"F0.imprint","INTERSECT",VERTEX,{"disambiguationData":[OD(0.0)],"derivedFrom":[subQ1,subQ0]});Q143=makeQuery(id+"F0.imprint","IMPRINT",FACE,{"disambiguationData":[TD([[makeQuery(id+"F0.imprint","IMPRINT",EDGE,{"disambiguationData":[TD([[subQ2,1.0]])],"derivedFrom":subQ1}),1.0]])]});}
            var Q144;
            {var subQ0=sQuery(id+"F0.wireOp",EDGE,"E1");var subQ1=sQuery(id+"F0.wireOp",EDGE,"E7.13.0");var subQ2=makeQuery(id+"F0.imprint","INTERSECT",VERTEX,{"disambiguationData":[OD(0.0)],"derivedFrom":[subQ1,subQ0]});Q144=makeQuery(id+"F0.imprint","IMPRINT",FACE,{"disambiguationData":[TD([[makeQuery(id+"F0.imprint","IMPRINT",EDGE,{"disambiguationData":[TD([[subQ2,1.0]])],"derivedFrom":subQ1}),1.0]])]});}
            var Q145;
            {var subQ0=sQuery(id+"F0.wireOp",EDGE,"E1");var subQ1=sQuery(id+"F0.wireOp",EDGE,"E7.16.0");var subQ2=makeQuery(id+"F0.imprint","INTERSECT",VERTEX,{"disambiguationData":[OD(0.0)],"derivedFrom":[subQ1,subQ0]});Q145=makeQuery(id+"F0.imprint","IMPRINT",FACE,{"disambiguationData":[TD([[makeQuery(id+"F0.imprint","IMPRINT",EDGE,{"disambiguationData":[TD([[subQ2,1.0]])],"derivedFrom":subQ1}),1.0]])]});}
            var Q146;
            {var subQ0=sQuery(id+"F0.wireOp",EDGE,"E0");var subQ1=sQuery(id+"F0.wireOp",EDGE,"E5.1.22.0");var subQ2=makeQuery(id+"F0.imprint","INTERSECT",VERTEX,{"disambiguationData":[OD(0.0)],"derivedFrom":[subQ1,subQ0]});Q146=makeQuery(id+"F0.imprint","IMPRINT",FACE,{"disambiguationData":[TD([[makeQuery(id+"F0.imprint","IMPRINT",EDGE,{"disambiguationData":[TD([[subQ2,-1.0]])],"derivedFrom":subQ1}),1.0]])]});}
            var Q147;
            {var subQ0=sQuery(id+"F0.wireOp",EDGE,"E1");var subQ1=sQuery(id+"F0.wireOp",EDGE,"E8.1.20.0");var subQ2=makeQuery(id+"F0.imprint","INTERSECT",VERTEX,{"disambiguationData":[OD(0.0)],"derivedFrom":[subQ1,subQ0]});Q147=makeQuery(id+"F0.imprint","IMPRINT",FACE,{"disambiguationData":[TD([[makeQuery(id+"F0.imprint","IMPRINT",EDGE,{"disambiguationData":[TD([[subQ2,1.0]])],"derivedFrom":subQ1}),1.0]])]});}
            var Q148;
            {var subQ0=sQuery(id+"F0.wireOp",EDGE,"E1");var subQ1=sQuery(id+"F0.wireOp",EDGE,"E8.1.31.0");var subQ2=makeQuery(id+"F0.imprint","INTERSECT",VERTEX,{"disambiguationData":[OD(0.0)],"derivedFrom":[subQ1,subQ0]});Q148=makeQuery(id+"F0.imprint","IMPRINT",FACE,{"disambiguationData":[TD([[makeQuery(id+"F0.imprint","IMPRINT",EDGE,{"disambiguationData":[TD([[subQ2,-1.0]])],"derivedFrom":subQ1}),1.0]])]});}
            var Q149;
            {var subQ0=sQuery(id+"F0.wireOp",EDGE,"E1");var subQ1=sQuery(id+"F0.wireOp",EDGE,"E8.1.35.0");var subQ2=makeQuery(id+"F0.imprint","INTERSECT",VERTEX,{"disambiguationData":[OD(0.0)],"derivedFrom":[subQ1,subQ0]});Q149=makeQuery(id+"F0.imprint","IMPRINT",FACE,{"disambiguationData":[TD([[makeQuery(id+"F0.imprint","IMPRINT",EDGE,{"disambiguationData":[TD([[subQ2,-1.0]])],"derivedFrom":subQ1}),1.0]])]});}
            var Q150;
            {var subQ0=sQuery(id+"F0.wireOp",EDGE,"E1");var subQ1=sQuery(id+"F0.wireOp",EDGE,"E8.1.34.0");var subQ2=makeQuery(id+"F0.imprint","INTERSECT",VERTEX,{"disambiguationData":[OD(0.0)],"derivedFrom":[subQ1,subQ0]});Q150=makeQuery(id+"F0.imprint","IMPRINT",FACE,{"disambiguationData":[TD([[makeQuery(id+"F0.imprint","IMPRINT",EDGE,{"disambiguationData":[TD([[subQ2,1.0]])],"derivedFrom":subQ1}),1.0]])]});}
            var Q151;
            {var subQ0=sQuery(id+"F0.wireOp",EDGE,"E1");var subQ1=sQuery(id+"F0.wireOp",EDGE,"E8.1.36.0");var subQ2=makeQuery(id+"F0.imprint","INTERSECT",VERTEX,{"disambiguationData":[OD(0.0)],"derivedFrom":[subQ1,subQ0]});Q151=makeQuery(id+"F0.imprint","IMPRINT",FACE,{"disambiguationData":[TD([[makeQuery(id+"F0.imprint","IMPRINT",EDGE,{"disambiguationData":[TD([[subQ2,1.0]])],"derivedFrom":subQ1}),1.0]])]});}
            var Q152;
            {var subQ0=sQuery(id+"F0.wireOp",EDGE,"E1");var subQ1=sQuery(id+"F0.wireOp",EDGE,"E7.12.0");var subQ2=makeQuery(id+"F0.imprint","INTERSECT",VERTEX,{"disambiguationData":[OD(0.0)],"derivedFrom":[subQ1,subQ0]});Q152=makeQuery(id+"F0.imprint","IMPRINT",FACE,{"disambiguationData":[TD([[makeQuery(id+"F0.imprint","IMPRINT",EDGE,{"disambiguationData":[TD([[subQ2,1.0]])],"derivedFrom":subQ1}),1.0]])]});}
            var Q153;
            {var subQ0=sQuery(id+"F0.wireOp",EDGE,"E1");var subQ1=sQuery(id+"F0.wireOp",EDGE,"E8.1.28.0");var subQ2=makeQuery(id+"F0.imprint","INTERSECT",VERTEX,{"disambiguationData":[OD(0.0)],"derivedFrom":[subQ1,subQ0]});Q153=makeQuery(id+"F0.imprint","IMPRINT",FACE,{"disambiguationData":[TD([[makeQuery(id+"F0.imprint","IMPRINT",EDGE,{"disambiguationData":[TD([[subQ2,1.0]])],"derivedFrom":subQ1}),1.0]])]});}
            var Q154;
            {var subQ0=sQuery(id+"F0.wireOp",EDGE,"E1");var subQ1=sQuery(id+"F0.wireOp",EDGE,"E8.1.20.0");var subQ2=makeQuery(id+"F0.imprint","INTERSECT",VERTEX,{"disambiguationData":[OD(0.0)],"derivedFrom":[subQ1,subQ0]});Q154=makeQuery(id+"F0.imprint","IMPRINT",FACE,{"disambiguationData":[TD([[makeQuery(id+"F0.imprint","IMPRINT",EDGE,{"disambiguationData":[TD([[subQ2,-1.0]])],"derivedFrom":subQ1}),1.0]])]});}
            var Q155;
            {var subQ0=sQuery(id+"F0.wireOp",EDGE,"E1");var subQ1=sQuery(id+"F0.wireOp",EDGE,"E7.7.0");var subQ2=makeQuery(id+"F0.imprint","INTERSECT",VERTEX,{"disambiguationData":[OD(0.0)],"derivedFrom":[subQ1,subQ0]});Q155=makeQuery(id+"F0.imprint","IMPRINT",FACE,{"disambiguationData":[TD([[makeQuery(id+"F0.imprint","IMPRINT",EDGE,{"disambiguationData":[TD([[subQ2,1.0]])],"derivedFrom":subQ1}),1.0]])]});}
            var Q156;
            {var subQ0=sQuery(id+"F0.wireOp",EDGE,"E0");var subQ1=sQuery(id+"F0.wireOp",EDGE,"E4.1.3.0");var subQ2=makeQuery(id+"F0.imprint","INTERSECT",VERTEX,{"disambiguationData":[OD(0.0)],"derivedFrom":[subQ1,subQ0]});Q156=makeQuery(id+"F0.imprint","IMPRINT",FACE,{"disambiguationData":[TD([[makeQuery(id+"F0.imprint","IMPRINT",EDGE,{"disambiguationData":[TD([[subQ2,-1.0]])],"derivedFrom":subQ1}),1.0]])]});}
            var Q157;
            {var subQ0=sQuery(id+"F0.wireOp",EDGE,"E1");var subQ1=sQuery(id+"F0.wireOp",EDGE,"E8.1.23.0");var subQ2=makeQuery(id+"F0.imprint","INTERSECT",VERTEX,{"disambiguationData":[OD(0.0)],"derivedFrom":[subQ1,subQ0]});Q157=makeQuery(id+"F0.imprint","IMPRINT",FACE,{"disambiguationData":[TD([[makeQuery(id+"F0.imprint","IMPRINT",EDGE,{"disambiguationData":[TD([[subQ2,-1.0]])],"derivedFrom":subQ1}),1.0]])]});}
            var Q158;
            {var subQ0=sQuery(id+"F0.wireOp",EDGE,"E1");var subQ1=sQuery(id+"F0.wireOp",EDGE,"E8.1.36.0");var subQ2=makeQuery(id+"F0.imprint","INTERSECT",VERTEX,{"disambiguationData":[OD(0.0)],"derivedFrom":[subQ1,subQ0]});Q158=makeQuery(id+"F0.imprint","IMPRINT",FACE,{"disambiguationData":[TD([[makeQuery(id+"F0.imprint","IMPRINT",EDGE,{"disambiguationData":[TD([[subQ2,-1.0]])],"derivedFrom":subQ1}),1.0]])]});}
            var Q159;
            {var subQ0=sQuery(id+"F0.wireOp",EDGE,"E0");var subQ1=sQuery(id+"F0.wireOp",EDGE,"E3.1.0");var subQ2=makeQuery(id+"F0.imprint","INTERSECT",VERTEX,{"disambiguationData":[OD(0.0)],"derivedFrom":[subQ1,subQ0]});Q159=makeQuery(id+"F0.imprint","IMPRINT",FACE,{"disambiguationData":[TD([[makeQuery(id+"F0.imprint","IMPRINT",EDGE,{"disambiguationData":[TD([[subQ2,-1.0]])],"derivedFrom":subQ1}),1.0]])]});}
            var Q160;
            {var subQ0=sQuery(id+"F0.wireOp",EDGE,"E5.1.26.0");var subQ1=sQuery(id+"F0.wireOp",EDGE,"E5.1.25.0");var subQ2=makeQuery(id+"F0.imprint","INTERSECT",VERTEX,{"disambiguationData":[OD(0.0)],"derivedFrom":[subQ1,subQ0]});Q160=makeQuery(id+"F0.imprint","IMPRINT",FACE,{"disambiguationData":[TD([[makeQuery(id+"F0.imprint","IMPRINT",EDGE,{"disambiguationData":[TD([[subQ2,-1.0]])],"derivedFrom":subQ1}),1.0]])]});}
            var Q161;
            {var subQ0=sQuery(id+"F0.wireOp",EDGE,"E1");var subQ1=sQuery(id+"F0.wireOp",EDGE,"E8.1.38.0");var subQ2=makeQuery(id+"F0.imprint","INTERSECT",VERTEX,{"disambiguationData":[OD(0.0)],"derivedFrom":[subQ1,subQ0]});Q161=makeQuery(id+"F0.imprint","IMPRINT",FACE,{"disambiguationData":[TD([[makeQuery(id+"F0.imprint","IMPRINT",EDGE,{"disambiguationData":[TD([[subQ2,1.0]])],"derivedFrom":subQ1}),1.0]])]});}
            var Q162;
            {var subQ0=sQuery(id+"F0.wireOp",EDGE,"E1");var subQ1=sQuery(id+"F0.wireOp",EDGE,"E8.1.33.0");var subQ2=makeQuery(id+"F0.imprint","INTERSECT",VERTEX,{"disambiguationData":[OD(0.0)],"derivedFrom":[subQ1,subQ0]});Q162=makeQuery(id+"F0.imprint","IMPRINT",FACE,{"disambiguationData":[TD([[makeQuery(id+"F0.imprint","IMPRINT",EDGE,{"disambiguationData":[TD([[subQ2,-1.0]])],"derivedFrom":subQ1}),1.0]])]});}
            var Q163;
            {var subQ0=sQuery(id+"F0.wireOp",EDGE,"E1");var subQ1=sQuery(id+"F0.wireOp",EDGE,"E7.14.0");var subQ2=makeQuery(id+"F0.imprint","INTERSECT",VERTEX,{"disambiguationData":[OD(0.0)],"derivedFrom":[subQ1,subQ0]});Q163=makeQuery(id+"F0.imprint","IMPRINT",FACE,{"disambiguationData":[TD([[makeQuery(id+"F0.imprint","IMPRINT",EDGE,{"disambiguationData":[TD([[subQ2,1.0]])],"derivedFrom":subQ1}),1.0]])]});}
            var Q164;
            {var subQ0=sQuery(id+"F0.wireOp",EDGE,"E1");var subQ1=sQuery(id+"F0.wireOp",EDGE,"E8.1.27.0");var subQ2=makeQuery(id+"F0.imprint","INTERSECT",VERTEX,{"disambiguationData":[OD(0.0)],"derivedFrom":[subQ1,subQ0]});Q164=makeQuery(id+"F0.imprint","IMPRINT",FACE,{"disambiguationData":[TD([[makeQuery(id+"F0.imprint","IMPRINT",EDGE,{"disambiguationData":[TD([[subQ2,1.0]])],"derivedFrom":subQ1}),1.0]])]});}
            var Q165;
            {var subQ0=sQuery(id+"F0.wireOp",EDGE,"E1");var subQ1=sQuery(id+"F0.wireOp",EDGE,"E7.6.0");var subQ2=makeQuery(id+"F0.imprint","INTERSECT",VERTEX,{"disambiguationData":[OD(0.0)],"derivedFrom":[subQ1,subQ0]});Q165=makeQuery(id+"F0.imprint","IMPRINT",FACE,{"disambiguationData":[TD([[makeQuery(id+"F0.imprint","IMPRINT",EDGE,{"disambiguationData":[TD([[subQ2,1.0]])],"derivedFrom":subQ1}),1.0]])]});}
            var Q166;
            {var subQ0=sQuery(id+"F0.wireOp",EDGE,"E1");var subQ1=sQuery(id+"F0.wireOp",EDGE,"E7.4.0");var subQ2=makeQuery(id+"F0.imprint","INTERSECT",VERTEX,{"disambiguationData":[OD(0.0)],"derivedFrom":[subQ1,subQ0]});Q166=makeQuery(id+"F0.imprint","IMPRINT",FACE,{"disambiguationData":[TD([[makeQuery(id+"F0.imprint","IMPRINT",EDGE,{"disambiguationData":[TD([[subQ2,1.0]])],"derivedFrom":subQ1}),1.0]])]});}
            var Q167;
            {var subQ0=sQuery(id+"F0.wireOp",EDGE,"E1");var subQ1=sQuery(id+"F0.wireOp",EDGE,"E7.2.0");var subQ2=makeQuery(id+"F0.imprint","INTERSECT",VERTEX,{"disambiguationData":[OD(0.0)],"derivedFrom":[subQ1,subQ0]});Q167=makeQuery(id+"F0.imprint","IMPRINT",FACE,{"disambiguationData":[TD([[makeQuery(id+"F0.imprint","IMPRINT",EDGE,{"disambiguationData":[TD([[subQ2,1.0]])],"derivedFrom":subQ1}),1.0]])]});}
            var Q168;
            {var subQ0=sQuery(id+"F0.wireOp",EDGE,"E0");var subQ1=sQuery(id+"F0.wireOp",EDGE,"E4.1.6.0");var subQ2=makeQuery(id+"F0.imprint","INTERSECT",VERTEX,{"disambiguationData":[OD(0.0)],"derivedFrom":[subQ1,subQ0]});Q168=makeQuery(id+"F0.imprint","IMPRINT",FACE,{"disambiguationData":[TD([[makeQuery(id+"F0.imprint","IMPRINT",EDGE,{"disambiguationData":[TD([[subQ2,-1.0]])],"derivedFrom":subQ1}),1.0]])]});}
            var Q169;
            {var subQ0=sQuery(id+"F0.wireOp",EDGE,"E1");var subQ1=sQuery(id+"F0.wireOp",EDGE,"E7.12.0");var subQ2=makeQuery(id+"F0.imprint","INTERSECT",VERTEX,{"disambiguationData":[OD(0.0)],"derivedFrom":[subQ1,subQ0]});Q169=makeQuery(id+"F0.imprint","IMPRINT",FACE,{"disambiguationData":[TD([[makeQuery(id+"F0.imprint","IMPRINT",EDGE,{"disambiguationData":[TD([[subQ2,-1.0]])],"derivedFrom":subQ1}),1.0]])]});}
            var Q170;
            {var subQ0=sQuery(id+"F0.wireOp",EDGE,"E5.1.15.0");var subQ1=sQuery(id+"F0.wireOp",EDGE,"E5.1.14.0");var subQ2=makeQuery(id+"F0.imprint","INTERSECT",VERTEX,{"disambiguationData":[OD(0.0)],"derivedFrom":[subQ1,subQ0]});Q170=makeQuery(id+"F0.imprint","IMPRINT",FACE,{"disambiguationData":[TD([[makeQuery(id+"F0.imprint","IMPRINT",EDGE,{"disambiguationData":[TD([[subQ2,-1.0]])],"derivedFrom":subQ1}),1.0]])]});}
            var Q171;
            {var subQ0=sQuery(id+"F0.wireOp",EDGE,"E5.1.18.0");var subQ1=sQuery(id+"F0.wireOp",EDGE,"E5.1.17.0");var subQ2=makeQuery(id+"F0.imprint","INTERSECT",VERTEX,{"disambiguationData":[OD(0.0)],"derivedFrom":[subQ1,subQ0]});Q171=makeQuery(id+"F0.imprint","IMPRINT",FACE,{"disambiguationData":[TD([[makeQuery(id+"F0.imprint","IMPRINT",EDGE,{"disambiguationData":[TD([[subQ2,-1.0]])],"derivedFrom":subQ1}),1.0]])]});}
            var Q172;
            {var subQ0=sQuery(id+"F0.wireOp",EDGE,"E0");var subQ1=sQuery(id+"F0.wireOp",EDGE,"E4.1.7.0");var subQ2=makeQuery(id+"F0.imprint","INTERSECT",VERTEX,{"disambiguationData":[OD(0.0)],"derivedFrom":[subQ1,subQ0]});Q172=makeQuery(id+"F0.imprint","IMPRINT",FACE,{"disambiguationData":[TD([[makeQuery(id+"F0.imprint","IMPRINT",EDGE,{"disambiguationData":[TD([[subQ2,-1.0]])],"derivedFrom":subQ1}),1.0]])]});}
            var Q173;
            {var subQ0=sQuery(id+"F0.wireOp",EDGE,"E3.2.0");var subQ1=sQuery(id+"F0.wireOp",EDGE,"E3.1.0");var subQ2=makeQuery(id+"F0.imprint","INTERSECT",VERTEX,{"disambiguationData":[OD(0.0)],"derivedFrom":[subQ1,subQ0]});Q173=makeQuery(id+"F0.imprint","IMPRINT",FACE,{"disambiguationData":[TD([[makeQuery(id+"F0.imprint","IMPRINT",EDGE,{"disambiguationData":[TD([[subQ2,-1.0]])],"derivedFrom":subQ1}),1.0]])]});}
            var Q174;
            {var subQ0=sQuery(id+"F0.wireOp",EDGE,"E4.1.5.0");var subQ1=sQuery(id+"F0.wireOp",EDGE,"E4.1.4.0");var subQ2=makeQuery(id+"F0.imprint","INTERSECT",VERTEX,{"disambiguationData":[OD(0.0)],"derivedFrom":[subQ1,subQ0]});Q174=makeQuery(id+"F0.imprint","IMPRINT",FACE,{"disambiguationData":[TD([[makeQuery(id+"F0.imprint","IMPRINT",EDGE,{"disambiguationData":[TD([[subQ2,-1.0]])],"derivedFrom":subQ1}),1.0]])]});}
            var Q175;
            {var subQ0=sQuery(id+"F0.wireOp",EDGE,"E4.1.4.0");var subQ1=sQuery(id+"F0.wireOp",EDGE,"E4.1.3.0");var subQ2=makeQuery(id+"F0.imprint","INTERSECT",VERTEX,{"disambiguationData":[OD(0.0)],"derivedFrom":[subQ1,subQ0]});Q175=makeQuery(id+"F0.imprint","IMPRINT",FACE,{"disambiguationData":[TD([[makeQuery(id+"F0.imprint","IMPRINT",EDGE,{"disambiguationData":[TD([[subQ2,-1.0]])],"derivedFrom":subQ1}),1.0]])]});}
            var Q176;
            {var subQ0=sQuery(id+"F0.wireOp",EDGE,"E4.1.3.0");var subQ1=sQuery(id+"F0.wireOp",EDGE,"E3.2.0");var subQ2=makeQuery(id+"F0.imprint","INTERSECT",VERTEX,{"disambiguationData":[OD(0.0)],"derivedFrom":[subQ1,subQ0]});Q176=makeQuery(id+"F0.imprint","IMPRINT",FACE,{"disambiguationData":[TD([[makeQuery(id+"F0.imprint","IMPRINT",EDGE,{"disambiguationData":[TD([[subQ2,-1.0]])],"derivedFrom":subQ1}),1.0]])]});}
            var Q177;
            {var subQ0=sQuery(id+"F0.wireOp",EDGE,"E0");var subQ1=sQuery(id+"F0.wireOp",EDGE,"E5.1.23.0");var subQ2=makeQuery(id+"F0.imprint","INTERSECT",VERTEX,{"disambiguationData":[OD(0.0)],"derivedFrom":[subQ1,subQ0]});Q177=makeQuery(id+"F0.imprint","IMPRINT",FACE,{"disambiguationData":[TD([[makeQuery(id+"F0.imprint","IMPRINT",EDGE,{"disambiguationData":[TD([[subQ2,-1.0]])],"derivedFrom":subQ1}),1.0]])]});}
            var Q178;
            {var subQ0=sQuery(id+"F0.wireOp",EDGE,"E5.1.30.0");var subQ1=sQuery(id+"F0.wireOp",EDGE,"E5.1.29.0");var subQ2=makeQuery(id+"F0.imprint","INTERSECT",VERTEX,{"disambiguationData":[OD(0.0)],"derivedFrom":[subQ1,subQ0]});Q178=makeQuery(id+"F0.imprint","IMPRINT",FACE,{"disambiguationData":[TD([[makeQuery(id+"F0.imprint","IMPRINT",EDGE,{"disambiguationData":[TD([[subQ2,-1.0]])],"derivedFrom":subQ1}),1.0]])]});}
            var Q179;
            {var subQ0=sQuery(id+"F0.wireOp",EDGE,"E5.1.22.0");var subQ1=sQuery(id+"F0.wireOp",EDGE,"E5.1.21.0");var subQ2=makeQuery(id+"F0.imprint","INTERSECT",VERTEX,{"disambiguationData":[OD(0.0)],"derivedFrom":[subQ1,subQ0]});Q179=makeQuery(id+"F0.imprint","IMPRINT",FACE,{"disambiguationData":[TD([[makeQuery(id+"F0.imprint","IMPRINT",EDGE,{"disambiguationData":[TD([[subQ2,-1.0]])],"derivedFrom":subQ1}),1.0]])]});}
            var Q180;
            {var subQ0=sQuery(id+"F0.wireOp",EDGE,"E4.1.6.0");var subQ1=sQuery(id+"F0.wireOp",EDGE,"E4.1.5.0");var subQ2=makeQuery(id+"F0.imprint","INTERSECT",VERTEX,{"disambiguationData":[OD(0.0)],"derivedFrom":[subQ1,subQ0]});Q180=makeQuery(id+"F0.imprint","IMPRINT",FACE,{"disambiguationData":[TD([[makeQuery(id+"F0.imprint","IMPRINT",EDGE,{"disambiguationData":[TD([[subQ2,-1.0]])],"derivedFrom":subQ1}),1.0]])]});}
            var Q181;
            {var subQ0=sQuery(id+"F0.wireOp",EDGE,"E0");var subQ1=sQuery(id+"F0.wireOp",EDGE,"E5.1.24.0");var subQ2=makeQuery(id+"F0.imprint","INTERSECT",VERTEX,{"disambiguationData":[OD(0.0)],"derivedFrom":[subQ1,subQ0]});Q181=makeQuery(id+"F0.imprint","IMPRINT",FACE,{"disambiguationData":[TD([[makeQuery(id+"F0.imprint","IMPRINT",EDGE,{"disambiguationData":[TD([[subQ2,-1.0]])],"derivedFrom":subQ1}),1.0]])]});}
            var Q182;
            {var subQ0=sQuery(id+"F0.wireOp",EDGE,"E4.1.9.0");var subQ1=sQuery(id+"F0.wireOp",EDGE,"E4.1.8.0");var subQ2=makeQuery(id+"F0.imprint","INTERSECT",VERTEX,{"disambiguationData":[OD(0.0)],"derivedFrom":[subQ1,subQ0]});Q182=makeQuery(id+"F0.imprint","IMPRINT",FACE,{"disambiguationData":[TD([[makeQuery(id+"F0.imprint","IMPRINT",EDGE,{"disambiguationData":[TD([[subQ2,-1.0]])],"derivedFrom":subQ1}),1.0]])]});}
            var Q183;
            {var subQ0=sQuery(id+"F0.wireOp",EDGE,"E0");var subQ1=sQuery(id+"F0.wireOp",EDGE,"E5.1.18.0");var subQ2=makeQuery(id+"F0.imprint","INTERSECT",VERTEX,{"disambiguationData":[OD(0.0)],"derivedFrom":[subQ1,subQ0]});Q183=makeQuery(id+"F0.imprint","IMPRINT",FACE,{"disambiguationData":[TD([[makeQuery(id+"F0.imprint","IMPRINT",EDGE,{"disambiguationData":[TD([[subQ2,-1.0]])],"derivedFrom":subQ1}),1.0]])]});}
            var Q184;
            {var subQ0=sQuery(id+"F0.wireOp",EDGE,"E5.1.21.0");var subQ1=sQuery(id+"F0.wireOp",EDGE,"E5.1.20.0");var subQ2=makeQuery(id+"F0.imprint","INTERSECT",VERTEX,{"disambiguationData":[OD(0.0)],"derivedFrom":[subQ1,subQ0]});Q184=makeQuery(id+"F0.imprint","IMPRINT",FACE,{"disambiguationData":[TD([[makeQuery(id+"F0.imprint","IMPRINT",EDGE,{"disambiguationData":[TD([[subQ2,-1.0]])],"derivedFrom":subQ1}),1.0]])]});}
            var Q185;
            {var subQ0=sQuery(id+"F0.wireOp",EDGE,"E5.1.17.0");var subQ1=sQuery(id+"F0.wireOp",EDGE,"E5.1.16.0");var subQ2=makeQuery(id+"F0.imprint","INTERSECT",VERTEX,{"disambiguationData":[OD(0.0)],"derivedFrom":[subQ1,subQ0]});Q185=makeQuery(id+"F0.imprint","IMPRINT",FACE,{"disambiguationData":[TD([[makeQuery(id+"F0.imprint","IMPRINT",EDGE,{"disambiguationData":[TD([[subQ2,-1.0]])],"derivedFrom":subQ1}),1.0]])]});}
            var Q186;
            {var subQ0=sQuery(id+"F0.wireOp",EDGE,"E3.1.0");var subQ1=sQuery(id+"F0.wireOp",EDGE,"E2");var subQ2=makeQuery(id+"F0.imprint","INTERSECT",VERTEX,{"disambiguationData":[OD(0.0)],"derivedFrom":[subQ1,subQ0]});Q186=makeQuery(id+"F0.imprint","IMPRINT",FACE,{"disambiguationData":[TD([[makeQuery(id+"F0.imprint","IMPRINT",EDGE,{"disambiguationData":[TD([[subQ2,-1.0]])],"derivedFrom":subQ1}),1.0]])]});}
            var Q187;
            {var subQ0=sQuery(id+"F0.wireOp",EDGE,"E5.1.23.0");var subQ1=sQuery(id+"F0.wireOp",EDGE,"E5.1.22.0");var subQ2=makeQuery(id+"F0.imprint","INTERSECT",VERTEX,{"disambiguationData":[OD(0.0)],"derivedFrom":[subQ1,subQ0]});Q187=makeQuery(id+"F0.imprint","IMPRINT",FACE,{"disambiguationData":[TD([[makeQuery(id+"F0.imprint","IMPRINT",EDGE,{"disambiguationData":[TD([[subQ2,-1.0]])],"derivedFrom":subQ1}),1.0]])]});}
            var Q188;
            {var subQ0=sQuery(id+"F0.wireOp",EDGE,"E5.1.31.0");var subQ1=sQuery(id+"F0.wireOp",EDGE,"E2");var subQ2=makeQuery(id+"F0.imprint","INTERSECT",VERTEX,{"disambiguationData":[OD(0.0)],"derivedFrom":[subQ1,subQ0]});Q188=makeQuery(id+"F0.imprint","IMPRINT",FACE,{"disambiguationData":[TD([[makeQuery(id+"F0.imprint","IMPRINT",EDGE,{"disambiguationData":[TD([[subQ2,1.0]])],"derivedFrom":subQ1}),1.0]])]});}
            var Q189;
            {var subQ0=sQuery(id+"F0.wireOp",EDGE,"E1");var subQ1=sQuery(id+"F0.wireOp",EDGE,"E7.4.0");var subQ2=makeQuery(id+"F0.imprint","INTERSECT",VERTEX,{"disambiguationData":[OD(0.0)],"derivedFrom":[subQ1,subQ0]});Q189=makeQuery(id+"F0.imprint","IMPRINT",FACE,{"disambiguationData":[TD([[makeQuery(id+"F0.imprint","IMPRINT",EDGE,{"disambiguationData":[TD([[subQ2,-1.0]])],"derivedFrom":subQ1}),1.0]])]});}
            var Q190;
            {var subQ0=sQuery(id+"F0.wireOp",EDGE,"E5.1.12.0");var subQ1=sQuery(id+"F0.wireOp",EDGE,"E5.1.11.0");var subQ2=makeQuery(id+"F0.imprint","INTERSECT",VERTEX,{"disambiguationData":[OD(0.0)],"derivedFrom":[subQ1,subQ0]});Q190=makeQuery(id+"F0.imprint","IMPRINT",FACE,{"disambiguationData":[TD([[makeQuery(id+"F0.imprint","IMPRINT",EDGE,{"disambiguationData":[TD([[subQ2,-1.0]])],"derivedFrom":subQ1}),1.0]])]});}
            var Q191;
            {var subQ0=sQuery(id+"F0.wireOp",EDGE,"E5.1.11.0");var subQ1=sQuery(id+"F0.wireOp",EDGE,"E5.1.10.0");var subQ2=makeQuery(id+"F0.imprint","INTERSECT",VERTEX,{"disambiguationData":[OD(0.0)],"derivedFrom":[subQ1,subQ0]});Q191=makeQuery(id+"F0.imprint","IMPRINT",FACE,{"disambiguationData":[TD([[makeQuery(id+"F0.imprint","IMPRINT",EDGE,{"disambiguationData":[TD([[subQ2,-1.0]])],"derivedFrom":subQ1}),1.0]])]});}
            var Q192;
            {var subQ0=sQuery(id+"F0.wireOp",EDGE,"E5.1.29.0");var subQ1=sQuery(id+"F0.wireOp",EDGE,"E5.1.28.0");var subQ2=makeQuery(id+"F0.imprint","INTERSECT",VERTEX,{"disambiguationData":[OD(0.0)],"derivedFrom":[subQ1,subQ0]});Q192=makeQuery(id+"F0.imprint","IMPRINT",FACE,{"disambiguationData":[TD([[makeQuery(id+"F0.imprint","IMPRINT",EDGE,{"disambiguationData":[TD([[subQ2,-1.0]])],"derivedFrom":subQ1}),1.0]])]});}
            var Q193;
            {var subQ0=sQuery(id+"F0.wireOp",EDGE,"E5.1.10.0");var subQ1=sQuery(id+"F0.wireOp",EDGE,"E4.1.9.0");var subQ2=makeQuery(id+"F0.imprint","INTERSECT",VERTEX,{"disambiguationData":[OD(0.0)],"derivedFrom":[subQ1,subQ0]});Q193=makeQuery(id+"F0.imprint","IMPRINT",FACE,{"disambiguationData":[TD([[makeQuery(id+"F0.imprint","IMPRINT",EDGE,{"disambiguationData":[TD([[subQ2,-1.0]])],"derivedFrom":subQ1}),1.0]])]});}
            var Q194;
            {var subQ0=sQuery(id+"F0.wireOp",EDGE,"E0");var subQ1=sQuery(id+"F0.wireOp",EDGE,"E5.1.19.0");var subQ2=makeQuery(id+"F0.imprint","INTERSECT",VERTEX,{"disambiguationData":[OD(0.0)],"derivedFrom":[subQ1,subQ0]});Q194=makeQuery(id+"F0.imprint","IMPRINT",FACE,{"disambiguationData":[TD([[makeQuery(id+"F0.imprint","IMPRINT",EDGE,{"disambiguationData":[TD([[subQ2,-1.0]])],"derivedFrom":subQ1}),1.0]])]});}
            var Q195;
            {var subQ0=sQuery(id+"F0.wireOp",EDGE,"E0");var subQ1=sQuery(id+"F0.wireOp",EDGE,"E5.1.17.0");var subQ2=makeQuery(id+"F0.imprint","INTERSECT",VERTEX,{"disambiguationData":[OD(0.0)],"derivedFrom":[subQ1,subQ0]});Q195=makeQuery(id+"F0.imprint","IMPRINT",FACE,{"disambiguationData":[TD([[makeQuery(id+"F0.imprint","IMPRINT",EDGE,{"disambiguationData":[TD([[subQ2,-1.0]])],"derivedFrom":subQ1}),1.0]])]});}
            var Q196;
            {var subQ0=sQuery(id+"F0.wireOp",EDGE,"E1");var subQ1=sQuery(id+"F0.wireOp",EDGE,"E8.1.39.0");var subQ2=makeQuery(id+"F0.imprint","INTERSECT",VERTEX,{"disambiguationData":[OD(0.0)],"derivedFrom":[subQ1,subQ0]});Q196=makeQuery(id+"F0.imprint","IMPRINT",FACE,{"disambiguationData":[TD([[makeQuery(id+"F0.imprint","IMPRINT",EDGE,{"disambiguationData":[TD([[subQ2,-1.0]])],"derivedFrom":subQ1}),1.0]])]});}
            var Q197;
            {var subQ0=sQuery(id+"F0.wireOp",EDGE,"E5.1.27.0");var subQ1=sQuery(id+"F0.wireOp",EDGE,"E5.1.26.0");var subQ2=makeQuery(id+"F0.imprint","INTERSECT",VERTEX,{"disambiguationData":[OD(0.0)],"derivedFrom":[subQ1,subQ0]});Q197=makeQuery(id+"F0.imprint","IMPRINT",FACE,{"disambiguationData":[TD([[makeQuery(id+"F0.imprint","IMPRINT",EDGE,{"disambiguationData":[TD([[subQ2,-1.0]])],"derivedFrom":subQ1}),1.0]])]});}
            var Q198;
            {var subQ0=sQuery(id+"F0.wireOp",EDGE,"E0");var subQ1=sQuery(id+"F0.wireOp",EDGE,"E5.1.25.0");var subQ2=makeQuery(id+"F0.imprint","INTERSECT",VERTEX,{"disambiguationData":[OD(0.0)],"derivedFrom":[subQ1,subQ0]});Q198=makeQuery(id+"F0.imprint","IMPRINT",FACE,{"disambiguationData":[TD([[makeQuery(id+"F0.imprint","IMPRINT",EDGE,{"disambiguationData":[TD([[subQ2,-1.0]])],"derivedFrom":subQ1}),1.0]])]});}
            var Q199;
            {var subQ0=sQuery(id+"F0.wireOp",EDGE,"E5.1.13.0");var subQ1=sQuery(id+"F0.wireOp",EDGE,"E5.1.12.0");var subQ2=makeQuery(id+"F0.imprint","INTERSECT",VERTEX,{"disambiguationData":[OD(0.0)],"derivedFrom":[subQ1,subQ0]});Q199=makeQuery(id+"F0.imprint","IMPRINT",FACE,{"disambiguationData":[TD([[makeQuery(id+"F0.imprint","IMPRINT",EDGE,{"disambiguationData":[TD([[subQ2,-1.0]])],"derivedFrom":subQ1}),1.0]])]});}
            var Q200;
            {var subQ0=sQuery(id+"F0.wireOp",EDGE,"E5.1.28.0");var subQ1=sQuery(id+"F0.wireOp",EDGE,"E5.1.27.0");var subQ2=makeQuery(id+"F0.imprint","INTERSECT",VERTEX,{"disambiguationData":[OD(0.0)],"derivedFrom":[subQ1,subQ0]});Q200=makeQuery(id+"F0.imprint","IMPRINT",FACE,{"disambiguationData":[TD([[makeQuery(id+"F0.imprint","IMPRINT",EDGE,{"disambiguationData":[TD([[subQ2,-1.0]])],"derivedFrom":subQ1}),1.0]])]});}
            var Q201;
            {var subQ0=sQuery(id+"F0.wireOp",EDGE,"E5.1.24.0");var subQ1=sQuery(id+"F0.wireOp",EDGE,"E5.1.23.0");var subQ2=makeQuery(id+"F0.imprint","INTERSECT",VERTEX,{"disambiguationData":[OD(0.0)],"derivedFrom":[subQ1,subQ0]});Q201=makeQuery(id+"F0.imprint","IMPRINT",FACE,{"disambiguationData":[TD([[makeQuery(id+"F0.imprint","IMPRINT",EDGE,{"disambiguationData":[TD([[subQ2,-1.0]])],"derivedFrom":subQ1}),1.0]])]});}
            var Q202;
            {var subQ0=sQuery(id+"F0.wireOp",EDGE,"E1");var subQ1=sQuery(id+"F0.wireOp",EDGE,"E7.18.0");var subQ2=makeQuery(id+"F0.imprint","INTERSECT",VERTEX,{"disambiguationData":[OD(0.0)],"derivedFrom":[subQ1,subQ0]});Q202=makeQuery(id+"F0.imprint","IMPRINT",FACE,{"disambiguationData":[TD([[makeQuery(id+"F0.imprint","IMPRINT",EDGE,{"disambiguationData":[TD([[subQ2,1.0]])],"derivedFrom":subQ1}),1.0]])]});}
            var Q203;
            {var subQ0=sQuery(id+"F0.wireOp",EDGE,"E0");var subQ1=sQuery(id+"F0.wireOp",EDGE,"E5.1.16.0");var subQ2=makeQuery(id+"F0.imprint","INTERSECT",VERTEX,{"disambiguationData":[OD(0.0)],"derivedFrom":[subQ1,subQ0]});Q203=makeQuery(id+"F0.imprint","IMPRINT",FACE,{"disambiguationData":[TD([[makeQuery(id+"F0.imprint","IMPRINT",EDGE,{"disambiguationData":[TD([[subQ2,-1.0]])],"derivedFrom":subQ1}),1.0]])]});}
            var Q204;
            {var subQ0=sQuery(id+"F0.wireOp",EDGE,"E0");var subQ1=sQuery(id+"F0.wireOp",EDGE,"E4.1.5.0");var subQ2=makeQuery(id+"F0.imprint","INTERSECT",VERTEX,{"disambiguationData":[OD(0.0)],"derivedFrom":[subQ1,subQ0]});Q204=makeQuery(id+"F0.imprint","IMPRINT",FACE,{"disambiguationData":[TD([[makeQuery(id+"F0.imprint","IMPRINT",EDGE,{"disambiguationData":[TD([[subQ2,-1.0]])],"derivedFrom":subQ1}),1.0]])]});}
            var Q205;
            {var subQ0=sQuery(id+"F0.wireOp",EDGE,"E4.1.8.0");var subQ1=sQuery(id+"F0.wireOp",EDGE,"E4.1.7.0");var subQ2=makeQuery(id+"F0.imprint","INTERSECT",VERTEX,{"disambiguationData":[OD(0.0)],"derivedFrom":[subQ1,subQ0]});Q205=makeQuery(id+"F0.imprint","IMPRINT",FACE,{"disambiguationData":[TD([[makeQuery(id+"F0.imprint","IMPRINT",EDGE,{"disambiguationData":[TD([[subQ2,-1.0]])],"derivedFrom":subQ1}),1.0]])]});}
            var Q206;
            {var subQ0=sQuery(id+"F0.wireOp",EDGE,"E1");var subQ1=sQuery(id+"F0.wireOp",EDGE,"E7.14.0");var subQ2=makeQuery(id+"F0.imprint","INTERSECT",VERTEX,{"disambiguationData":[OD(0.0)],"derivedFrom":[subQ1,subQ0]});Q206=makeQuery(id+"F0.imprint","IMPRINT",FACE,{"disambiguationData":[TD([[makeQuery(id+"F0.imprint","IMPRINT",EDGE,{"disambiguationData":[TD([[subQ2,-1.0]])],"derivedFrom":subQ1}),1.0]])]});}
            var Q207;
            {var subQ0=sQuery(id+"F0.wireOp",EDGE,"E1");var subQ1=sQuery(id+"F0.wireOp",EDGE,"E7.5.0");var subQ2=makeQuery(id+"F0.imprint","INTERSECT",VERTEX,{"disambiguationData":[OD(0.0)],"derivedFrom":[subQ1,subQ0]});Q207=makeQuery(id+"F0.imprint","IMPRINT",FACE,{"disambiguationData":[TD([[makeQuery(id+"F0.imprint","IMPRINT",EDGE,{"disambiguationData":[TD([[subQ2,-1.0]])],"derivedFrom":subQ1}),1.0]])]});}
            var Q208;
            {var subQ0=sQuery(id+"F0.wireOp",EDGE,"E1");var subQ1=sQuery(id+"F0.wireOp",EDGE,"E7.2.0");var subQ2=makeQuery(id+"F0.imprint","INTERSECT",VERTEX,{"disambiguationData":[OD(0.0)],"derivedFrom":[subQ1,subQ0]});Q208=makeQuery(id+"F0.imprint","IMPRINT",FACE,{"disambiguationData":[TD([[makeQuery(id+"F0.imprint","IMPRINT",EDGE,{"disambiguationData":[TD([[subQ2,-1.0]])],"derivedFrom":subQ1}),1.0]])]});}
            extrude(context, id + "F1", {"entities" : qUnion([Q0, Q1, Q2, Q3, Q4, Q5, Q6, Q7, Q8, Q9, Q10, Q11, Q12, Q13, Q14, Q15, Q16, Q17, Q18, Q19, Q20, Q21, Q22, Q23, Q24, Q25, Q26, Q27, Q28, Q29, Q30, Q31, Q32, Q33, Q34, Q35, Q36, Q37, Q38, Q39, Q40, Q41, Q42, Q43, Q44, Q45, Q46, Q47, Q48, Q49, Q50, Q51, Q52, Q53, Q54, Q55, Q56, Q57, Q58, Q59, Q60, Q61, Q62, Q63, Q64, Q65, Q66, Q67, Q68, Q69, Q70, Q71, Q72, Q73, Q74, Q75, Q76, Q77, Q78, Q79, Q80, Q81, Q82, Q83, Q84, Q85, Q86, Q87, Q88, Q89, Q90, Q91, Q92, Q93, Q94, Q95, Q96, Q97, Q98, Q99, Q100, Q101, Q102, Q103, Q104, Q105, Q106, Q107, Q108, Q109, Q110, Q111, Q112, Q113, Q114, Q115, Q116, Q117, Q118, Q119, Q120, Q121, Q122, Q123, Q124, Q125, Q126, Q127, Q128, Q129, Q130, Q131, Q132, Q133, Q134, Q135, Q136, Q137, Q138, Q139, Q140, Q141, Q142, Q143, Q144, Q145, Q146, Q147, Q148, Q149, Q150, Q151, Q152, Q153, Q154, Q155, Q156, Q157, Q158, Q159, Q160, Q161, Q162, Q163, Q164, Q165, Q166, Q167, Q168, Q169, Q170, Q171, Q172, Q173, Q174, Q175, Q176, Q177, Q178, Q179, Q180, Q181, Q182, Q183, Q184, Q185, Q186, Q187, Q188, Q189, Q190, Q191, Q192, Q193, Q194, Q195, Q196, Q197, Q198, Q199, Q200, Q201, Q202, Q203, Q204, Q205, Q206, Q207, Q208]), "depth" : 4 * mm, "offsetDistance" : 25 * mm});
        }
        {
            var Q0;
            Q0=makeQuery(id+"F1.opExtrude","CAP_FACE",FACE,{"disambiguationData":[OSD([sQuery(id+"F0.wireOp",EDGE,"E2"),sQuery(id+"F0.wireOp",EDGE,"E3.1.0"),sQuery(id+"F0.wireOp",EDGE,"E3.2.0"),sQuery(id+"F0.wireOp",EDGE,"E4.1.3.0"),sQuery(id+"F0.wireOp",EDGE,"E4.1.4.0"),sQuery(id+"F0.wireOp",EDGE,"E4.1.5.0"),sQuery(id+"F0.wireOp",EDGE,"E4.1.6.0"),sQuery(id+"F0.wireOp",EDGE,"E4.1.7.0"),sQuery(id+"F0.wireOp",EDGE,"E4.1.8.0"),sQuery(id+"F0.wireOp",EDGE,"E4.1.9.0"),sQuery(id+"F0.wireOp",EDGE,"E5.1.10.0"),sQuery(id+"F0.wireOp",EDGE,"E5.1.11.0"),sQuery(id+"F0.wireOp",EDGE,"E5.1.12.0"),sQuery(id+"F0.wireOp",EDGE,"E5.1.13.0"),sQuery(id+"F0.wireOp",EDGE,"E5.1.14.0"),sQuery(id+"F0.wireOp",EDGE,"E5.1.15.0"),sQuery(id+"F0.wireOp",EDGE,"E5.1.16.0"),sQuery(id+"F0.wireOp",EDGE,"E5.1.17.0"),sQuery(id+"F0.wireOp",EDGE,"E5.1.18.0"),sQuery(id+"F0.wireOp",EDGE,"E5.1.19.0"),sQuery(id+"F0.wireOp",EDGE,"E5.1.20.0"),sQuery(id+"F0.wireOp",EDGE,"E5.1.21.0"),sQuery(id+"F0.wireOp",EDGE,"E5.1.22.0"),sQuery(id+"F0.wireOp",EDGE,"E5.1.23.0"),sQuery(id+"F0.wireOp",EDGE,"E5.1.24.0"),sQuery(id+"F0.wireOp",EDGE,"E5.1.25.0"),sQuery(id+"F0.wireOp",EDGE,"E5.1.26.0"),sQuery(id+"F0.wireOp",EDGE,"E5.1.27.0"),sQuery(id+"F0.wireOp",EDGE,"E5.1.28.0"),sQuery(id+"F0.wireOp",EDGE,"E5.1.29.0"),sQuery(id+"F0.wireOp",EDGE,"E5.1.30.0"),sQuery(id+"F0.wireOp",EDGE,"E5.1.31.0"),sQuery(id+"F0.wireOp",EDGE,"E6"),sQuery(id+"F0.wireOp",EDGE,"E7.1.0"),sQuery(id+"F0.wireOp",EDGE,"E7.2.0"),sQuery(id+"F0.wireOp",EDGE,"E7.3.0"),sQuery(id+"F0.wireOp",EDGE,"E7.4.0"),sQuery(id+"F0.wireOp",EDGE,"E7.5.0"),sQuery(id+"F0.wireOp",EDGE,"E7.6.0"),sQuery(id+"F0.wireOp",EDGE,"E7.7.0"),sQuery(id+"F0.wireOp",EDGE,"E7.8.0"),sQuery(id+"F0.wireOp",EDGE,"E7.9.0"),sQuery(id+"F0.wireOp",EDGE,"E7.10.0"),sQuery(id+"F0.wireOp",EDGE,"E7.11.0"),sQuery(id+"F0.wireOp",EDGE,"E7.12.0"),sQuery(id+"F0.wireOp",EDGE,"E7.13.0"),sQuery(id+"F0.wireOp",EDGE,"E7.14.0"),sQuery(id+"F0.wireOp",EDGE,"E7.15.0"),sQuery(id+"F0.wireOp",EDGE,"E7.16.0"),sQuery(id+"F0.wireOp",EDGE,"E7.17.0"),sQuery(id+"F0.wireOp",EDGE,"E7.18.0"),sQuery(id+"F0.wireOp",EDGE,"E7.19.0"),sQuery(id+"F0.wireOp",EDGE,"E8.1.20.0"),sQuery(id+"F0.wireOp",EDGE,"E8.1.21.0"),sQuery(id+"F0.wireOp",EDGE,"E8.1.22.0"),sQuery(id+"F0.wireOp",EDGE,"E8.1.23.0"),sQuery(id+"F0.wireOp",EDGE,"E8.1.24.0"),sQuery(id+"F0.wireOp",EDGE,"E8.1.25.0"),sQuery(id+"F0.wireOp",EDGE,"E8.1.26.0"),sQuery(id+"F0.wireOp",EDGE,"E8.1.27.0"),sQuery(id+"F0.wireOp",EDGE,"E8.1.28.0"),sQuery(id+"F0.wireOp",EDGE,"E8.1.29.0"),sQuery(id+"F0.wireOp",EDGE,"E8.1.30.0"),sQuery(id+"F0.wireOp",EDGE,"E8.1.31.0"),sQuery(id+"F0.wireOp",EDGE,"E8.1.32.0"),sQuery(id+"F0.wireOp",EDGE,"E8.1.33.0"),sQuery(id+"F0.wireOp",EDGE,"E8.1.34.0"),sQuery(id+"F0.wireOp",EDGE,"E8.1.35.0"),sQuery(id+"F0.wireOp",EDGE,"E8.1.36.0"),sQuery(id+"F0.wireOp",EDGE,"E8.1.37.0"),sQuery(id+"F0.wireOp",EDGE,"E8.1.38.0"),sQuery(id+"F0.wireOp",EDGE,"E8.1.39.0"),sQuery(id+"F0.wireOp",EDGE,"E1")])],"isStart":false});
            var sketch = newSketch(context, id + "F2", { "sketchPlane" : qUnion([Q0])});
            skPoint(sketch, "E9", {"position": v(0, 0) * mm});
            skCircle(sketch, "E10", {"center": v(0, 0) * mm, "radius": 4 * mm});
            skCircle(sketch, "E11", {"center": v(0, 0) * mm, "radius": 3.25 * mm});
            skSolve(sketch);
        }
        {
            var Q0;
            Q0=makeQuery(id+"F2.imprint","IMPRINT",FACE,{"disambiguationData":[TD([[makeQuery(id+"F2.imprint","IMPRINT",EDGE,{"derivedFrom":sQuery(id+"F2.wireOp",EDGE,"E10")}),1.0]])]});
            extrude(context, id + "F3", {"entities" : qUnion([Q0]), "operationType" : NewBodyOperationType.REMOVE, "oppositeDirection" : true, "depth" : 0.6 * mm, "offsetDistance" : 25 * mm});
        }
        {
            var Q0;
            Q0=makeQuery(id+"F3.boolean.opBoolean","COPY",EDGE,{"derivedFrom":makeQuery(id+"F3.opExtrude","CAP_EDGE",EDGE,{"disambiguationData":[OSD([sQuery(id+"F2.wireOp",EDGE,"E10")])],"isStart":true})});
            var Q1;
            Q1=makeQuery(id+"F3.boolean.opBoolean","COPY",EDGE,{"derivedFrom":makeQuery(id+"F3.opExtrude","CAP_EDGE",EDGE,{"disambiguationData":[OSD([sQuery(id+"F2.wireOp",EDGE,"E11")])],"isStart":true})});
            fillet(context, id + "F4", {"entities" : qUnion([Q0, Q1]), "radius" : 0.6 * mm, "tangentPropagation" : true, "allowEdgeOverflow" : false});
        }
    });
